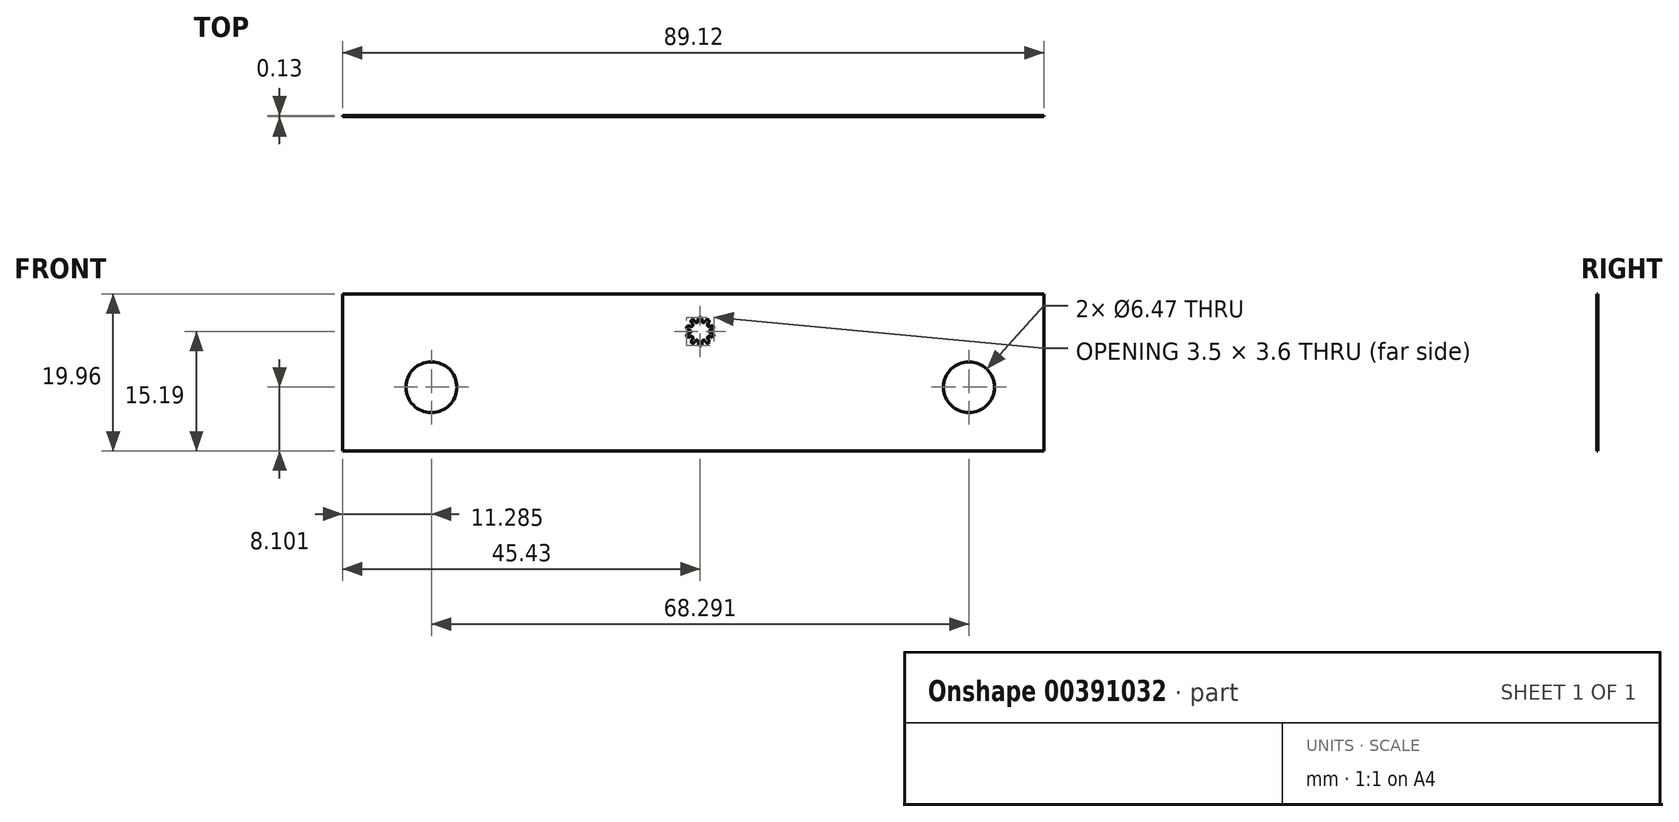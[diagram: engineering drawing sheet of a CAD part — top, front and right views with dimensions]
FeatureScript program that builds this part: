
annotation { "Feature Type Name" : "Feature", "Feature Type Description" : "" }
export const myFeature = defineFeature(function(context is Context, id is Id, definition is map)
    precondition{}
    {
        {
            var Q0;
            Q0=qCreatedBy(makeId("Front.planeOp"),FACE);
            var sketch = newSketch(context, id + "F0", { "sketchPlane" : qUnion([Q0])});
            skLineSegment(sketch, "E0.bottom", {"start": v(-45.43, -15.2) * mm, "end": v(43.7, -15.2) * mm});
            skLineSegment(sketch, "E0.top", {"start": v(-45.43, 4.77) * mm, "end": v(43.7, 4.77) * mm});
            skLineSegment(sketch, "E0.left", {"start": v(-45.43, -15.2) * mm, "end": v(-45.43, 4.77) * mm});
            skLineSegment(sketch, "E0.right", {"start": v(43.7, -15.2) * mm, "end": v(43.7, 4.77) * mm});
            skCircle(sketch, "E1", {"center": v(-34.15, -7.09) * mm, "radius": 3.24 * mm});
            skCircle(sketch, "E2.MirrorC", {"center": v(34.15, -7.09) * mm, "radius": 3.24 * mm});
            skCircle(sketch, "E3", {"center": v(0, 0) * mm, "radius": 0.5 * mm});
            skLineSegment(sketch, "E4", {"start": v(0.64, 1.31) * mm, "end": v(0.64, 1.3) * mm});
            skLineSegment(sketch, "E5", {"start": v(0.64, 1.3) * mm, "end": v(0.64, 1.3) * mm});
            skLineSegment(sketch, "E6", {"start": v(0.64, 1.3) * mm, "end": v(0.63, 1.3) * mm});
            skLineSegment(sketch, "E7", {"start": v(0.63, 1.3) * mm, "end": v(0.63, 1.3) * mm});
            skLineSegment(sketch, "E8", {"start": v(0.63, 1.3) * mm, "end": v(0.62, 1.29) * mm});
            skLineSegment(sketch, "E9", {"start": v(0.62, 1.29) * mm, "end": v(0.62, 1.28) * mm});
            skLineSegment(sketch, "E10", {"start": v(0.62, 1.28) * mm, "end": v(0.62, 1.28) * mm});
            skLineSegment(sketch, "E11", {"start": v(0.62, 1.28) * mm, "end": v(0.61, 1.27) * mm});
            skLineSegment(sketch, "E12", {"start": v(0.61, 1.27) * mm, "end": v(0.61, 1.27) * mm});
            skLineSegment(sketch, "E13", {"start": v(0.61, 1.27) * mm, "end": v(0.54, 1.16) * mm});
            skArc(sketch, "E14", {"start": v(0.54, 1.16) * mm, "mid": v(0.48, 1.12) * mm, "end": v(0.42, 1.12) * mm});
            skArc(sketch, "E15", {"start": v(0.42, 1.12) * mm, "mid": v(0.36, 1.15) * mm, "end": v(0.3, 1.16) * mm});
            skArc(sketch, "E16", {"start": v(0.3, 1.16) * mm, "mid": v(0.24, 1.2) * mm, "end": v(0.22, 1.26) * mm});
            skLineSegment(sketch, "E17", {"start": v(0.22, 1.26) * mm, "end": v(0.22, 1.4) * mm});
            skLineSegment(sketch, "E18", {"start": v(0.22, 1.4) * mm, "end": v(0.22, 1.4) * mm});
            skLineSegment(sketch, "E19", {"start": v(0.22, 1.4) * mm, "end": v(0.22, 1.41) * mm});
            skLineSegment(sketch, "E20", {"start": v(0.22, 1.41) * mm, "end": v(0.22, 1.42) * mm});
            skLineSegment(sketch, "E21", {"start": v(0.22, 1.42) * mm, "end": v(0.22, 1.42) * mm});
            skLineSegment(sketch, "E22", {"start": v(0.22, 1.42) * mm, "end": v(0.22, 1.43) * mm});
            skLineSegment(sketch, "E23", {"start": v(0.22, 1.43) * mm, "end": v(0.22, 1.43) * mm});
            skLineSegment(sketch, "E24", {"start": v(0.22, 1.43) * mm, "end": v(0.22, 1.44) * mm});
            skLineSegment(sketch, "E25", {"start": v(0.22, 1.44) * mm, "end": v(0.22, 1.44) * mm});
            skLineSegment(sketch, "E26", {"start": v(0.22, 1.44) * mm, "end": v(0.22, 1.45) * mm});
            skLineSegment(sketch, "E27", {"start": v(0.22, 1.45) * mm, "end": v(0.22, 1.46) * mm});
            skLineSegment(sketch, "E28", {"start": v(0.22, 1.46) * mm, "end": v(0.22, 1.46) * mm});
            skLineSegment(sketch, "E29", {"start": v(0.22, 1.46) * mm, "end": v(0.22, 1.47) * mm});
            skLineSegment(sketch, "E30", {"start": v(0.22, 1.47) * mm, "end": v(0.22, 1.47) * mm});
            skLineSegment(sketch, "E31", {"start": v(0.22, 1.47) * mm, "end": v(0.22, 1.48) * mm});
            skLineSegment(sketch, "E32", {"start": v(0.22, 1.48) * mm, "end": v(0.22, 1.49) * mm});
            skLineSegment(sketch, "E33", {"start": v(0.22, 1.49) * mm, "end": v(0.22, 1.5) * mm});
            skLineSegment(sketch, "E34", {"start": v(0.22, 1.5) * mm, "end": v(0.22, 1.5) * mm});
            skLineSegment(sketch, "E35", {"start": v(0.22, 1.5) * mm, "end": v(0.22, 1.51) * mm});
            skLineSegment(sketch, "E36", {"start": v(0.22, 1.51) * mm, "end": v(0.22, 1.52) * mm});
            skLineSegment(sketch, "E37", {"start": v(0.22, 1.52) * mm, "end": v(0.22, 1.53) * mm});
            skLineSegment(sketch, "E38", {"start": v(0.22, 1.53) * mm, "end": v(0.22, 1.54) * mm});
            skLineSegment(sketch, "E39", {"start": v(0.22, 1.54) * mm, "end": v(0.21, 1.55) * mm});
            skLineSegment(sketch, "E40", {"start": v(0.21, 1.55) * mm, "end": v(0.21, 1.56) * mm});
            skLineSegment(sketch, "E41", {"start": v(0.21, 1.56) * mm, "end": v(0.2, 1.57) * mm});
            skLineSegment(sketch, "E42", {"start": v(0.2, 1.57) * mm, "end": v(0.2, 1.58) * mm});
            skLineSegment(sketch, "E43", {"start": v(0.2, 1.58) * mm, "end": v(0.2, 1.59) * mm});
            skLineSegment(sketch, "E44", {"start": v(0.2, 1.59) * mm, "end": v(0.2, 1.6) * mm});
            skLineSegment(sketch, "E45", {"start": v(0.2, 1.6) * mm, "end": v(0.2, 1.61) * mm});
            skLineSegment(sketch, "E46", {"start": v(0.2, 1.61) * mm, "end": v(0.19, 1.62) * mm});
            skLineSegment(sketch, "E47", {"start": v(0.19, 1.62) * mm, "end": v(0.18, 1.64) * mm});
            skLineSegment(sketch, "E48", {"start": v(0.18, 1.64) * mm, "end": v(0.17, 1.65) * mm});
            skLineSegment(sketch, "E49", {"start": v(0.17, 1.65) * mm, "end": v(0.17, 1.67) * mm});
            skLineSegment(sketch, "E50", {"start": v(0.17, 1.67) * mm, "end": v(0.16, 1.7) * mm});
            skLineSegment(sketch, "E51", {"start": v(0.16, 1.7) * mm, "end": v(0.14, 1.71) * mm});
            skLineSegment(sketch, "E52", {"start": v(0.14, 1.71) * mm, "end": v(0.13, 1.74) * mm});
            skLineSegment(sketch, "E53", {"start": v(0.13, 1.74) * mm, "end": v(0.1, 1.77) * mm});
            skLineSegment(sketch, "E54", {"start": v(0.1, 1.77) * mm, "end": v(0.1, 1.8) * mm});
            skArc(sketch, "E55", {"start": v(0.1, 1.8) * mm, "mid": v(-0.02, 1.8) * mm, "end": v(-0.13, 1.8) * mm});
            skLineSegment(sketch, "E56", {"start": v(-0.13, 1.8) * mm, "end": v(-0.15, 1.77) * mm});
            skLineSegment(sketch, "E57", {"start": v(-0.15, 1.77) * mm, "end": v(-0.17, 1.74) * mm});
            skLineSegment(sketch, "E58", {"start": v(-0.17, 1.74) * mm, "end": v(-0.18, 1.7) * mm});
            skLineSegment(sketch, "E59", {"start": v(-0.18, 1.7) * mm, "end": v(-0.2, 1.69) * mm});
            skLineSegment(sketch, "E60", {"start": v(-0.2, 1.69) * mm, "end": v(-0.2, 1.67) * mm});
            skLineSegment(sketch, "E61", {"start": v(-0.2, 1.67) * mm, "end": v(-0.21, 1.65) * mm});
            skLineSegment(sketch, "E62", {"start": v(-0.21, 1.65) * mm, "end": v(-0.22, 1.63) * mm});
            skLineSegment(sketch, "E63", {"start": v(-0.22, 1.63) * mm, "end": v(-0.22, 1.62) * mm});
            skLineSegment(sketch, "E64", {"start": v(-0.22, 1.62) * mm, "end": v(-0.23, 1.6) * mm});
            skLineSegment(sketch, "E65", {"start": v(-0.23, 1.6) * mm, "end": v(-0.23, 1.6) * mm});
            skLineSegment(sketch, "E66", {"start": v(-0.23, 1.6) * mm, "end": v(-0.24, 1.58) * mm});
            skLineSegment(sketch, "E67", {"start": v(-0.24, 1.58) * mm, "end": v(-0.24, 1.57) * mm});
            skLineSegment(sketch, "E68", {"start": v(-0.24, 1.57) * mm, "end": v(-0.24, 1.56) * mm});
            skLineSegment(sketch, "E69", {"start": v(-0.24, 1.56) * mm, "end": v(-0.25, 1.55) * mm});
            skLineSegment(sketch, "E70", {"start": v(-0.25, 1.55) * mm, "end": v(-0.25, 1.54) * mm});
            skLineSegment(sketch, "E71", {"start": v(-0.25, 1.54) * mm, "end": v(-0.25, 1.53) * mm});
            skLineSegment(sketch, "E72", {"start": v(-0.25, 1.53) * mm, "end": v(-0.25, 1.53) * mm});
            skLineSegment(sketch, "E73", {"start": v(-0.25, 1.53) * mm, "end": v(-0.25, 1.52) * mm});
            skLineSegment(sketch, "E74", {"start": v(-0.25, 1.52) * mm, "end": v(-0.25, 1.5) * mm});
            skLineSegment(sketch, "E75", {"start": v(-0.25, 1.5) * mm, "end": v(-0.25, 1.5) * mm});
            skLineSegment(sketch, "E76", {"start": v(-0.25, 1.5) * mm, "end": v(-0.25, 1.48) * mm});
            skLineSegment(sketch, "E77", {"start": v(-0.25, 1.48) * mm, "end": v(-0.25, 1.48) * mm});
            skLineSegment(sketch, "E78", {"start": v(-0.25, 1.48) * mm, "end": v(-0.25, 1.47) * mm});
            skLineSegment(sketch, "E79", {"start": v(-0.25, 1.47) * mm, "end": v(-0.25, 1.46) * mm});
            skLineSegment(sketch, "E80", {"start": v(-0.25, 1.46) * mm, "end": v(-0.25, 1.46) * mm});
            skLineSegment(sketch, "E81", {"start": v(-0.25, 1.46) * mm, "end": v(-0.25, 1.45) * mm});
            skLineSegment(sketch, "E82", {"start": v(-0.25, 1.45) * mm, "end": v(-0.25, 1.44) * mm});
            skLineSegment(sketch, "E83", {"start": v(-0.25, 1.44) * mm, "end": v(-0.25, 1.44) * mm});
            skLineSegment(sketch, "E84", {"start": v(-0.25, 1.44) * mm, "end": v(-0.25, 1.43) * mm});
            skLineSegment(sketch, "E85", {"start": v(-0.25, 1.43) * mm, "end": v(-0.25, 1.43) * mm});
            skLineSegment(sketch, "E86", {"start": v(-0.25, 1.43) * mm, "end": v(-0.25, 1.42) * mm});
            skLineSegment(sketch, "E87", {"start": v(-0.25, 1.42) * mm, "end": v(-0.25, 1.42) * mm});
            skLineSegment(sketch, "E88", {"start": v(-0.25, 1.42) * mm, "end": v(-0.25, 1.41) * mm});
            skLineSegment(sketch, "E89", {"start": v(-0.25, 1.41) * mm, "end": v(-0.25, 1.4) * mm});
            skLineSegment(sketch, "E90", {"start": v(-0.25, 1.4) * mm, "end": v(-0.25, 1.4) * mm});
            skLineSegment(sketch, "E91", {"start": v(-0.25, 1.4) * mm, "end": v(-0.25, 1.39) * mm});
            skLineSegment(sketch, "E92", {"start": v(-0.25, 1.39) * mm, "end": v(-0.25, 1.25) * mm});
            skArc(sketch, "E93", {"start": v(-0.25, 1.25) * mm, "mid": v(-0.27, 1.2) * mm, "end": v(-0.32, 1.16) * mm});
            skArc(sketch, "E94", {"start": v(-0.32, 1.16) * mm, "mid": v(-0.38, 1.14) * mm, "end": v(-0.44, 1.11) * mm});
            skArc(sketch, "E95", {"start": v(-0.44, 1.11) * mm, "mid": v(-0.5, 1.11) * mm, "end": v(-0.56, 1.15) * mm});
            skLineSegment(sketch, "E96", {"start": v(-0.56, 1.15) * mm, "end": v(-0.64, 1.25) * mm});
            skLineSegment(sketch, "E97", {"start": v(-0.64, 1.25) * mm, "end": v(-0.64, 1.26) * mm});
            skLineSegment(sketch, "E98", {"start": v(-0.64, 1.26) * mm, "end": v(-0.64, 1.26) * mm});
            skLineSegment(sketch, "E99", {"start": v(-0.64, 1.26) * mm, "end": v(-0.65, 1.26) * mm});
            skLineSegment(sketch, "E100", {"start": v(-0.65, 1.26) * mm, "end": v(-0.65, 1.27) * mm});
            skLineSegment(sketch, "E101", {"start": v(-0.65, 1.27) * mm, "end": v(-0.65, 1.27) * mm});
            skLineSegment(sketch, "E102", {"start": v(-0.65, 1.27) * mm, "end": v(-0.65, 1.28) * mm});
            skLineSegment(sketch, "E103", {"start": v(-0.65, 1.28) * mm, "end": v(-0.66, 1.28) * mm});
            skLineSegment(sketch, "E104", {"start": v(-0.66, 1.28) * mm, "end": v(-0.66, 1.28) * mm});
            skLineSegment(sketch, "E105", {"start": v(-0.66, 1.28) * mm, "end": v(-0.66, 1.29) * mm});
            skLineSegment(sketch, "E106", {"start": v(-0.66, 1.29) * mm, "end": v(-0.67, 1.3) * mm});
            skLineSegment(sketch, "E107", {"start": v(-0.67, 1.3) * mm, "end": v(-0.67, 1.3) * mm});
            skLineSegment(sketch, "E108", {"start": v(-0.67, 1.3) * mm, "end": v(-0.68, 1.3) * mm});
            skLineSegment(sketch, "E109", {"start": v(-0.68, 1.3) * mm, "end": v(-0.68, 1.31) * mm});
            skLineSegment(sketch, "E110", {"start": v(-0.68, 1.31) * mm, "end": v(-0.69, 1.32) * mm});
            skLineSegment(sketch, "E111", {"start": v(-0.69, 1.32) * mm, "end": v(-0.7, 1.32) * mm});
            skLineSegment(sketch, "E112", {"start": v(-0.7, 1.32) * mm, "end": v(-0.7, 1.33) * mm});
            skLineSegment(sketch, "E113", {"start": v(-0.7, 1.33) * mm, "end": v(-0.7, 1.33) * mm});
            skLineSegment(sketch, "E114", {"start": v(-0.7, 1.33) * mm, "end": v(-0.7, 1.34) * mm});
            skLineSegment(sketch, "E115", {"start": v(-0.7, 1.34) * mm, "end": v(-0.7, 1.35) * mm});
            skLineSegment(sketch, "E116", {"start": v(-0.7, 1.35) * mm, "end": v(-0.71, 1.35) * mm});
            skLineSegment(sketch, "E117", {"start": v(-0.71, 1.35) * mm, "end": v(-0.72, 1.36) * mm});
            skLineSegment(sketch, "E118", {"start": v(-0.72, 1.36) * mm, "end": v(-0.72, 1.37) * mm});
            skLineSegment(sketch, "E119", {"start": v(-0.72, 1.37) * mm, "end": v(-0.73, 1.37) * mm});
            skLineSegment(sketch, "E120", {"start": v(-0.73, 1.37) * mm, "end": v(-0.74, 1.38) * mm});
            skLineSegment(sketch, "E121", {"start": v(-0.74, 1.38) * mm, "end": v(-0.74, 1.39) * mm});
            skLineSegment(sketch, "E122", {"start": v(-0.74, 1.39) * mm, "end": v(-0.75, 1.4) * mm});
            skLineSegment(sketch, "E123", {"start": v(-0.75, 1.4) * mm, "end": v(-0.76, 1.4) * mm});
            skLineSegment(sketch, "E124", {"start": v(-0.76, 1.4) * mm, "end": v(-0.77, 1.4) * mm});
            skLineSegment(sketch, "E125", {"start": v(-0.77, 1.4) * mm, "end": v(-0.78, 1.41) * mm});
            skLineSegment(sketch, "E126", {"start": v(-0.78, 1.41) * mm, "end": v(-0.8, 1.42) * mm});
            skLineSegment(sketch, "E127", {"start": v(-0.8, 1.42) * mm, "end": v(-0.8, 1.42) * mm});
            skLineSegment(sketch, "E128", {"start": v(-0.8, 1.42) * mm, "end": v(-0.82, 1.43) * mm});
            skLineSegment(sketch, "E129", {"start": v(-0.82, 1.43) * mm, "end": v(-0.83, 1.44) * mm});
            skLineSegment(sketch, "E130", {"start": v(-0.83, 1.44) * mm, "end": v(-0.85, 1.45) * mm});
            skLineSegment(sketch, "E131", {"start": v(-0.85, 1.45) * mm, "end": v(-0.87, 1.46) * mm});
            skLineSegment(sketch, "E132", {"start": v(-0.87, 1.46) * mm, "end": v(-0.9, 1.47) * mm});
            skLineSegment(sketch, "E133", {"start": v(-0.9, 1.47) * mm, "end": v(-0.92, 1.48) * mm});
            skLineSegment(sketch, "E134", {"start": v(-0.92, 1.48) * mm, "end": v(-0.95, 1.5) * mm});
            skLineSegment(sketch, "E135", {"start": v(-0.95, 1.5) * mm, "end": v(-0.98, 1.5) * mm});
            skArc(sketch, "E136", {"start": v(-0.98, 1.5) * mm, "mid": v(-1.07, 1.44) * mm, "end": v(-1.16, 1.38) * mm});
            skLineSegment(sketch, "E137", {"start": v(-1.16, 1.38) * mm, "end": v(-1.16, 1.34) * mm});
            skLineSegment(sketch, "E138", {"start": v(-1.16, 1.34) * mm, "end": v(-1.15, 1.3) * mm});
            skLineSegment(sketch, "E139", {"start": v(-1.15, 1.3) * mm, "end": v(-1.15, 1.28) * mm});
            skLineSegment(sketch, "E140", {"start": v(-1.15, 1.28) * mm, "end": v(-1.15, 1.25) * mm});
            skLineSegment(sketch, "E141", {"start": v(-1.15, 1.25) * mm, "end": v(-1.14, 1.23) * mm});
            skLineSegment(sketch, "E142", {"start": v(-1.14, 1.23) * mm, "end": v(-1.14, 1.21) * mm});
            skLineSegment(sketch, "E143", {"start": v(-1.14, 1.21) * mm, "end": v(-1.14, 1.2) * mm});
            skLineSegment(sketch, "E144", {"start": v(-1.14, 1.2) * mm, "end": v(-1.13, 1.18) * mm});
            skLineSegment(sketch, "E145", {"start": v(-1.13, 1.18) * mm, "end": v(-1.13, 1.17) * mm});
            skLineSegment(sketch, "E146", {"start": v(-1.13, 1.17) * mm, "end": v(-1.13, 1.15) * mm});
            skLineSegment(sketch, "E147", {"start": v(-1.13, 1.15) * mm, "end": v(-1.12, 1.14) * mm});
            skLineSegment(sketch, "E148", {"start": v(-1.12, 1.14) * mm, "end": v(-1.12, 1.13) * mm});
            skLineSegment(sketch, "E149", {"start": v(-1.12, 1.13) * mm, "end": v(-1.12, 1.12) * mm});
            skLineSegment(sketch, "E150", {"start": v(-1.12, 1.12) * mm, "end": v(-1.11, 1.11) * mm});
            skLineSegment(sketch, "E151", {"start": v(-1.11, 1.11) * mm, "end": v(-1.1, 1.1) * mm});
            skLineSegment(sketch, "E152", {"start": v(-1.1, 1.1) * mm, "end": v(-1.1, 1.1) * mm});
            skLineSegment(sketch, "E153", {"start": v(-1.1, 1.1) * mm, "end": v(-1.1, 1.09) * mm});
            skLineSegment(sketch, "E154", {"start": v(-1.1, 1.09) * mm, "end": v(-1.1, 1.08) * mm});
            skLineSegment(sketch, "E155", {"start": v(-1.1, 1.08) * mm, "end": v(-1.1, 1.07) * mm});
            skLineSegment(sketch, "E156", {"start": v(-1.1, 1.07) * mm, "end": v(-1.09, 1.07) * mm});
            skLineSegment(sketch, "E157", {"start": v(-1.09, 1.07) * mm, "end": v(-1.08, 1.06) * mm});
            skLineSegment(sketch, "E158", {"start": v(-1.08, 1.06) * mm, "end": v(-1.08, 1.05) * mm});
            skLineSegment(sketch, "E159", {"start": v(-1.08, 1.05) * mm, "end": v(-1.07, 1.05) * mm});
            skLineSegment(sketch, "E160", {"start": v(-1.07, 1.05) * mm, "end": v(-1.07, 1.04) * mm});
            skLineSegment(sketch, "E161", {"start": v(-1.07, 1.04) * mm, "end": v(-1.06, 1.04) * mm});
            skLineSegment(sketch, "E162", {"start": v(-1.06, 1.04) * mm, "end": v(-1.06, 1.03) * mm});
            skLineSegment(sketch, "E163", {"start": v(-1.06, 1.03) * mm, "end": v(-1.06, 1.03) * mm});
            skLineSegment(sketch, "E164", {"start": v(-1.06, 1.03) * mm, "end": v(-1.05, 1.02) * mm});
            skLineSegment(sketch, "E165", {"start": v(-1.05, 1.02) * mm, "end": v(-1.05, 1.02) * mm});
            skLineSegment(sketch, "E166", {"start": v(-1.05, 1.02) * mm, "end": v(-1.05, 1.01) * mm});
            skLineSegment(sketch, "E167", {"start": v(-1.05, 1.01) * mm, "end": v(-1.04, 1) * mm});
            skLineSegment(sketch, "E168", {"start": v(-1.04, 1) * mm, "end": v(-1.04, 1) * mm});
            skLineSegment(sketch, "E169", {"start": v(-1.04, 1) * mm, "end": v(-1.03, 1) * mm});
            skLineSegment(sketch, "E170", {"start": v(-1.03, 1) * mm, "end": v(-1.03, 1) * mm});
            skLineSegment(sketch, "E171", {"start": v(-1.03, 1) * mm, "end": v(-1.03, 0.99) * mm});
            skLineSegment(sketch, "E172", {"start": v(-1.03, 0.99) * mm, "end": v(-1.02, 0.98) * mm});
            skLineSegment(sketch, "E173", {"start": v(-1.02, 0.98) * mm, "end": v(-1.02, 0.98) * mm});
            skLineSegment(sketch, "E174", {"start": v(-1.02, 0.98) * mm, "end": v(-1.02, 0.97) * mm});
            skLineSegment(sketch, "E175", {"start": v(-1.02, 0.97) * mm, "end": v(-0.94, 0.87) * mm});
            skArc(sketch, "E176", {"start": v(-0.94, 0.87) * mm, "mid": v(-0.92, 0.8) * mm, "end": v(-0.94, 0.75) * mm});
            skArc(sketch, "E177", {"start": v(-0.94, 0.75) * mm, "mid": v(-0.98, 0.7) * mm, "end": v(-1.01, 0.64) * mm});
            skArc(sketch, "E178", {"start": v(-1.01, 0.64) * mm, "mid": v(-1.06, 0.6) * mm, "end": v(-1.13, 0.6) * mm});
            skLineSegment(sketch, "E179", {"start": v(-1.13, 0.6) * mm, "end": v(-1.26, 0.64) * mm});
            skLineSegment(sketch, "E180", {"start": v(-1.26, 0.64) * mm, "end": v(-1.26, 0.64) * mm});
            skLineSegment(sketch, "E181", {"start": v(-1.26, 0.64) * mm, "end": v(-1.27, 0.64) * mm});
            skLineSegment(sketch, "E182", {"start": v(-1.27, 0.64) * mm, "end": v(-1.27, 0.64) * mm});
            skLineSegment(sketch, "E183", {"start": v(-1.27, 0.64) * mm, "end": v(-1.28, 0.65) * mm});
            skLineSegment(sketch, "E184", {"start": v(-1.28, 0.65) * mm, "end": v(-1.28, 0.65) * mm});
            skLineSegment(sketch, "E185", {"start": v(-1.28, 0.65) * mm, "end": v(-1.29, 0.65) * mm});
            skLineSegment(sketch, "E186", {"start": v(-1.29, 0.65) * mm, "end": v(-1.3, 0.65) * mm});
            skLineSegment(sketch, "E187", {"start": v(-1.3, 0.65) * mm, "end": v(-1.3, 0.65) * mm});
            skLineSegment(sketch, "E188", {"start": v(-1.3, 0.65) * mm, "end": v(-1.3, 0.66) * mm});
            skLineSegment(sketch, "E189", {"start": v(-1.3, 0.66) * mm, "end": v(-1.31, 0.66) * mm});
            skLineSegment(sketch, "E190", {"start": v(-1.31, 0.66) * mm, "end": v(-1.32, 0.66) * mm});
            skLineSegment(sketch, "E191", {"start": v(-1.32, 0.66) * mm, "end": v(-1.32, 0.66) * mm});
            skLineSegment(sketch, "E192", {"start": v(-1.32, 0.66) * mm, "end": v(-1.33, 0.66) * mm});
            skLineSegment(sketch, "E193", {"start": v(-1.33, 0.66) * mm, "end": v(-1.34, 0.66) * mm});
            skLineSegment(sketch, "E194", {"start": v(-1.34, 0.66) * mm, "end": v(-1.34, 0.67) * mm});
            skLineSegment(sketch, "E195", {"start": v(-1.34, 0.67) * mm, "end": v(-1.35, 0.67) * mm});
            skLineSegment(sketch, "E196", {"start": v(-1.35, 0.67) * mm, "end": v(-1.36, 0.67) * mm});
            skLineSegment(sketch, "E197", {"start": v(-1.36, 0.67) * mm, "end": v(-1.36, 0.67) * mm});
            skLineSegment(sketch, "E198", {"start": v(-1.36, 0.67) * mm, "end": v(-1.37, 0.68) * mm});
            skLineSegment(sketch, "E199", {"start": v(-1.37, 0.68) * mm, "end": v(-1.38, 0.68) * mm});
            skLineSegment(sketch, "E200", {"start": v(-1.38, 0.68) * mm, "end": v(-1.39, 0.68) * mm});
            skLineSegment(sketch, "E201", {"start": v(-1.39, 0.68) * mm, "end": v(-1.4, 0.68) * mm});
            skLineSegment(sketch, "E202", {"start": v(-1.4, 0.68) * mm, "end": v(-1.4, 0.68) * mm});
            skLineSegment(sketch, "E203", {"start": v(-1.4, 0.68) * mm, "end": v(-1.42, 0.68) * mm});
            skLineSegment(sketch, "E204", {"start": v(-1.42, 0.68) * mm, "end": v(-1.43, 0.68) * mm});
            skLineSegment(sketch, "E205", {"start": v(-1.43, 0.68) * mm, "end": v(-1.44, 0.68) * mm});
            skLineSegment(sketch, "E206", {"start": v(-1.44, 0.68) * mm, "end": v(-1.45, 0.68) * mm});
            skLineSegment(sketch, "E207", {"start": v(-1.45, 0.68) * mm, "end": v(-1.46, 0.68) * mm});
            skLineSegment(sketch, "E208", {"start": v(-1.46, 0.68) * mm, "end": v(-1.47, 0.68) * mm});
            skLineSegment(sketch, "E209", {"start": v(-1.47, 0.68) * mm, "end": v(-1.49, 0.68) * mm});
            skLineSegment(sketch, "E210", {"start": v(-1.49, 0.68) * mm, "end": v(-1.5, 0.68) * mm});
            skLineSegment(sketch, "E211", {"start": v(-1.5, 0.68) * mm, "end": v(-1.52, 0.68) * mm});
            skLineSegment(sketch, "E212", {"start": v(-1.52, 0.68) * mm, "end": v(-1.54, 0.67) * mm});
            skLineSegment(sketch, "E213", {"start": v(-1.54, 0.67) * mm, "end": v(-1.56, 0.67) * mm});
            skLineSegment(sketch, "E214", {"start": v(-1.56, 0.67) * mm, "end": v(-1.59, 0.67) * mm});
            skLineSegment(sketch, "E215", {"start": v(-1.59, 0.67) * mm, "end": v(-1.62, 0.66) * mm});
            skLineSegment(sketch, "E216", {"start": v(-1.62, 0.66) * mm, "end": v(-1.65, 0.65) * mm});
            skLineSegment(sketch, "E217", {"start": v(-1.65, 0.65) * mm, "end": v(-1.68, 0.64) * mm});
            skArc(sketch, "E218", {"start": v(-1.68, 0.64) * mm, "mid": v(-1.72, 0.54) * mm, "end": v(-1.75, 0.43) * mm});
            skLineSegment(sketch, "E219", {"start": v(-1.75, 0.43) * mm, "end": v(-1.73, 0.4) * mm});
            skLineSegment(sketch, "E220", {"start": v(-1.73, 0.4) * mm, "end": v(-1.7, 0.38) * mm});
            skLineSegment(sketch, "E221", {"start": v(-1.7, 0.38) * mm, "end": v(-1.68, 0.36) * mm});
            skLineSegment(sketch, "E222", {"start": v(-1.68, 0.36) * mm, "end": v(-1.66, 0.34) * mm});
            skLineSegment(sketch, "E223", {"start": v(-1.66, 0.34) * mm, "end": v(-1.65, 0.32) * mm});
            skLineSegment(sketch, "E224", {"start": v(-1.65, 0.32) * mm, "end": v(-1.63, 0.3) * mm});
            skLineSegment(sketch, "E225", {"start": v(-1.63, 0.3) * mm, "end": v(-1.62, 0.3) * mm});
            skLineSegment(sketch, "E226", {"start": v(-1.62, 0.3) * mm, "end": v(-1.61, 0.29) * mm});
            skLineSegment(sketch, "E227", {"start": v(-1.61, 0.29) * mm, "end": v(-1.6, 0.28) * mm});
            skLineSegment(sketch, "E228", {"start": v(-1.6, 0.28) * mm, "end": v(-1.59, 0.27) * mm});
            skLineSegment(sketch, "E229", {"start": v(-1.59, 0.27) * mm, "end": v(-1.58, 0.26) * mm});
            skLineSegment(sketch, "E230", {"start": v(-1.58, 0.26) * mm, "end": v(-1.57, 0.26) * mm});
            skLineSegment(sketch, "E231", {"start": v(-1.57, 0.26) * mm, "end": v(-1.56, 0.25) * mm});
            skLineSegment(sketch, "E232", {"start": v(-1.56, 0.25) * mm, "end": v(-1.55, 0.25) * mm});
            skLineSegment(sketch, "E233", {"start": v(-1.55, 0.25) * mm, "end": v(-1.54, 0.24) * mm});
            skLineSegment(sketch, "E234", {"start": v(-1.54, 0.24) * mm, "end": v(-1.54, 0.24) * mm});
            skLineSegment(sketch, "E235", {"start": v(-1.54, 0.24) * mm, "end": v(-1.53, 0.23) * mm});
            skLineSegment(sketch, "E236", {"start": v(-1.53, 0.23) * mm, "end": v(-1.52, 0.23) * mm});
            skLineSegment(sketch, "E237", {"start": v(-1.52, 0.23) * mm, "end": v(-1.51, 0.23) * mm});
            skLineSegment(sketch, "E238", {"start": v(-1.51, 0.23) * mm, "end": v(-1.5, 0.22) * mm});
            skLineSegment(sketch, "E239", {"start": v(-1.5, 0.22) * mm, "end": v(-1.5, 0.22) * mm});
            skLineSegment(sketch, "E240", {"start": v(-1.5, 0.22) * mm, "end": v(-1.49, 0.22) * mm});
            skLineSegment(sketch, "E241", {"start": v(-1.49, 0.22) * mm, "end": v(-1.48, 0.22) * mm});
            skLineSegment(sketch, "E242", {"start": v(-1.48, 0.22) * mm, "end": v(-1.48, 0.22) * mm});
            skLineSegment(sketch, "E243", {"start": v(-1.48, 0.22) * mm, "end": v(-1.47, 0.21) * mm});
            skLineSegment(sketch, "E244", {"start": v(-1.47, 0.21) * mm, "end": v(-1.46, 0.21) * mm});
            skLineSegment(sketch, "E245", {"start": v(-1.46, 0.21) * mm, "end": v(-1.46, 0.2) * mm});
            skLineSegment(sketch, "E246", {"start": v(-1.46, 0.2) * mm, "end": v(-1.45, 0.2) * mm});
            skLineSegment(sketch, "E247", {"start": v(-1.45, 0.2) * mm, "end": v(-1.45, 0.2) * mm});
            skLineSegment(sketch, "E248", {"start": v(-1.45, 0.2) * mm, "end": v(-1.44, 0.2) * mm});
            skLineSegment(sketch, "E249", {"start": v(-1.44, 0.2) * mm, "end": v(-1.44, 0.2) * mm});
            skLineSegment(sketch, "E250", {"start": v(-1.44, 0.2) * mm, "end": v(-1.43, 0.2) * mm});
            skLineSegment(sketch, "E251", {"start": v(-1.43, 0.2) * mm, "end": v(-1.43, 0.2) * mm});
            skLineSegment(sketch, "E252", {"start": v(-1.43, 0.2) * mm, "end": v(-1.42, 0.2) * mm});
            skLineSegment(sketch, "E253", {"start": v(-1.42, 0.2) * mm, "end": v(-1.42, 0.2) * mm});
            skLineSegment(sketch, "E254", {"start": v(-1.42, 0.2) * mm, "end": v(-1.41, 0.2) * mm});
            skLineSegment(sketch, "E255", {"start": v(-1.41, 0.2) * mm, "end": v(-1.4, 0.2) * mm});
            skLineSegment(sketch, "E256", {"start": v(-1.4, 0.2) * mm, "end": v(-1.4, 0.2) * mm});
            skLineSegment(sketch, "E257", {"start": v(-1.4, 0.2) * mm, "end": v(-1.27, 0.15) * mm});
            skArc(sketch, "E258", {"start": v(-1.27, 0.15) * mm, "mid": v(-1.22, 0.11) * mm, "end": v(-1.2, 0.05) * mm});
            skArc(sketch, "E259", {"start": v(-1.2, 0.05) * mm, "mid": v(-1.2, -0.01) * mm, "end": v(-1.2, -0.08) * mm});
            skArc(sketch, "E260", {"start": v(-1.2, -0.08) * mm, "mid": v(-1.21, -0.14) * mm, "end": v(-1.27, -0.18) * mm});
            skLineSegment(sketch, "E261", {"start": v(-1.27, -0.18) * mm, "end": v(-1.4, -0.22) * mm});
            skLineSegment(sketch, "E262", {"start": v(-1.4, -0.22) * mm, "end": v(-1.4, -0.22) * mm});
            skLineSegment(sketch, "E263", {"start": v(-1.4, -0.22) * mm, "end": v(-1.4, -0.23) * mm});
            skLineSegment(sketch, "E264", {"start": v(-1.4, -0.23) * mm, "end": v(-1.41, -0.23) * mm});
            skLineSegment(sketch, "E265", {"start": v(-1.41, -0.23) * mm, "end": v(-1.42, -0.23) * mm});
            skLineSegment(sketch, "E266", {"start": v(-1.42, -0.23) * mm, "end": v(-1.42, -0.23) * mm});
            skLineSegment(sketch, "E267", {"start": v(-1.42, -0.23) * mm, "end": v(-1.43, -0.23) * mm});
            skLineSegment(sketch, "E268", {"start": v(-1.43, -0.23) * mm, "end": v(-1.43, -0.23) * mm});
            skLineSegment(sketch, "E269", {"start": v(-1.43, -0.23) * mm, "end": v(-1.44, -0.24) * mm});
            skLineSegment(sketch, "E270", {"start": v(-1.44, -0.24) * mm, "end": v(-1.44, -0.24) * mm});
            skLineSegment(sketch, "E271", {"start": v(-1.44, -0.24) * mm, "end": v(-1.45, -0.24) * mm});
            skLineSegment(sketch, "E272", {"start": v(-1.45, -0.24) * mm, "end": v(-1.45, -0.24) * mm});
            skLineSegment(sketch, "E273", {"start": v(-1.45, -0.24) * mm, "end": v(-1.46, -0.24) * mm});
            skLineSegment(sketch, "E274", {"start": v(-1.46, -0.24) * mm, "end": v(-1.46, -0.25) * mm});
            skLineSegment(sketch, "E275", {"start": v(-1.46, -0.25) * mm, "end": v(-1.47, -0.25) * mm});
            skLineSegment(sketch, "E276", {"start": v(-1.47, -0.25) * mm, "end": v(-1.48, -0.25) * mm});
            skLineSegment(sketch, "E277", {"start": v(-1.48, -0.25) * mm, "end": v(-1.48, -0.25) * mm});
            skLineSegment(sketch, "E278", {"start": v(-1.48, -0.25) * mm, "end": v(-1.5, -0.25) * mm});
            skLineSegment(sketch, "E279", {"start": v(-1.5, -0.25) * mm, "end": v(-1.5, -0.26) * mm});
            skLineSegment(sketch, "E280", {"start": v(-1.5, -0.26) * mm, "end": v(-1.5, -0.26) * mm});
            skLineSegment(sketch, "E281", {"start": v(-1.5, -0.26) * mm, "end": v(-1.51, -0.26) * mm});
            skLineSegment(sketch, "E282", {"start": v(-1.51, -0.26) * mm, "end": v(-1.52, -0.27) * mm});
            skLineSegment(sketch, "E283", {"start": v(-1.52, -0.27) * mm, "end": v(-1.53, -0.27) * mm});
            skLineSegment(sketch, "E284", {"start": v(-1.53, -0.27) * mm, "end": v(-1.54, -0.27) * mm});
            skLineSegment(sketch, "E285", {"start": v(-1.54, -0.27) * mm, "end": v(-1.55, -0.28) * mm});
            skLineSegment(sketch, "E286", {"start": v(-1.55, -0.28) * mm, "end": v(-1.56, -0.28) * mm});
            skLineSegment(sketch, "E287", {"start": v(-1.56, -0.28) * mm, "end": v(-1.56, -0.3) * mm});
            skLineSegment(sketch, "E288", {"start": v(-1.56, -0.3) * mm, "end": v(-1.57, -0.3) * mm});
            skLineSegment(sketch, "E289", {"start": v(-1.57, -0.3) * mm, "end": v(-1.58, -0.3) * mm});
            skLineSegment(sketch, "E290", {"start": v(-1.58, -0.3) * mm, "end": v(-1.6, -0.31) * mm});
            skLineSegment(sketch, "E291", {"start": v(-1.6, -0.31) * mm, "end": v(-1.6, -0.32) * mm});
            skLineSegment(sketch, "E292", {"start": v(-1.6, -0.32) * mm, "end": v(-1.61, -0.33) * mm});
            skLineSegment(sketch, "E293", {"start": v(-1.61, -0.33) * mm, "end": v(-1.63, -0.35) * mm});
            skLineSegment(sketch, "E294", {"start": v(-1.63, -0.35) * mm, "end": v(-1.64, -0.36) * mm});
            skLineSegment(sketch, "E295", {"start": v(-1.64, -0.36) * mm, "end": v(-1.66, -0.37) * mm});
            skLineSegment(sketch, "E296", {"start": v(-1.66, -0.37) * mm, "end": v(-1.67, -0.4) * mm});
            skLineSegment(sketch, "E297", {"start": v(-1.67, -0.4) * mm, "end": v(-1.7, -0.42) * mm});
            skLineSegment(sketch, "E298", {"start": v(-1.7, -0.42) * mm, "end": v(-1.72, -0.44) * mm});
            skLineSegment(sketch, "E299", {"start": v(-1.72, -0.44) * mm, "end": v(-1.74, -0.47) * mm});
            skArc(sketch, "E300", {"start": v(-1.74, -0.47) * mm, "mid": v(-1.7, -0.57) * mm, "end": v(-1.67, -0.68) * mm});
            skLineSegment(sketch, "E301", {"start": v(-1.67, -0.68) * mm, "end": v(-1.63, -0.69) * mm});
            skLineSegment(sketch, "E302", {"start": v(-1.63, -0.69) * mm, "end": v(-1.6, -0.7) * mm});
            skLineSegment(sketch, "E303", {"start": v(-1.6, -0.7) * mm, "end": v(-1.57, -0.7) * mm});
            skLineSegment(sketch, "E304", {"start": v(-1.57, -0.7) * mm, "end": v(-1.54, -0.7) * mm});
            skLineSegment(sketch, "E305", {"start": v(-1.54, -0.7) * mm, "end": v(-1.52, -0.7) * mm});
            skLineSegment(sketch, "E306", {"start": v(-1.52, -0.7) * mm, "end": v(-1.5, -0.71) * mm});
            skLineSegment(sketch, "E307", {"start": v(-1.5, -0.71) * mm, "end": v(-1.49, -0.71) * mm});
            skLineSegment(sketch, "E308", {"start": v(-1.49, -0.71) * mm, "end": v(-1.47, -0.71) * mm});
            skLineSegment(sketch, "E309", {"start": v(-1.47, -0.71) * mm, "end": v(-1.46, -0.71) * mm});
            skLineSegment(sketch, "E310", {"start": v(-1.46, -0.71) * mm, "end": v(-1.44, -0.71) * mm});
            skLineSegment(sketch, "E311", {"start": v(-1.44, -0.71) * mm, "end": v(-1.43, -0.72) * mm});
            skLineSegment(sketch, "E312", {"start": v(-1.43, -0.72) * mm, "end": v(-1.42, -0.72) * mm});
            skLineSegment(sketch, "E313", {"start": v(-1.42, -0.72) * mm, "end": v(-1.41, -0.72) * mm});
            skLineSegment(sketch, "E314", {"start": v(-1.41, -0.72) * mm, "end": v(-1.4, -0.71) * mm});
            skLineSegment(sketch, "E315", {"start": v(-1.4, -0.71) * mm, "end": v(-1.4, -0.71) * mm});
            skLineSegment(sketch, "E316", {"start": v(-1.4, -0.71) * mm, "end": v(-1.38, -0.71) * mm});
            skLineSegment(sketch, "E317", {"start": v(-1.38, -0.71) * mm, "end": v(-1.37, -0.71) * mm});
            skLineSegment(sketch, "E318", {"start": v(-1.37, -0.71) * mm, "end": v(-1.36, -0.7) * mm});
            skLineSegment(sketch, "E319", {"start": v(-1.36, -0.7) * mm, "end": v(-1.36, -0.7) * mm});
            skLineSegment(sketch, "E320", {"start": v(-1.36, -0.7) * mm, "end": v(-1.35, -0.7) * mm});
            skLineSegment(sketch, "E321", {"start": v(-1.35, -0.7) * mm, "end": v(-1.34, -0.7) * mm});
            skLineSegment(sketch, "E322", {"start": v(-1.34, -0.7) * mm, "end": v(-1.33, -0.7) * mm});
            skLineSegment(sketch, "E323", {"start": v(-1.33, -0.7) * mm, "end": v(-1.33, -0.7) * mm});
            skLineSegment(sketch, "E324", {"start": v(-1.33, -0.7) * mm, "end": v(-1.32, -0.7) * mm});
            skLineSegment(sketch, "E325", {"start": v(-1.32, -0.7) * mm, "end": v(-1.31, -0.7) * mm});
            skLineSegment(sketch, "E326", {"start": v(-1.31, -0.7) * mm, "end": v(-1.3, -0.69) * mm});
            skLineSegment(sketch, "E327", {"start": v(-1.3, -0.69) * mm, "end": v(-1.3, -0.69) * mm});
            skLineSegment(sketch, "E328", {"start": v(-1.3, -0.69) * mm, "end": v(-1.3, -0.68) * mm});
            skLineSegment(sketch, "E329", {"start": v(-1.3, -0.68) * mm, "end": v(-1.29, -0.68) * mm});
            skLineSegment(sketch, "E330", {"start": v(-1.29, -0.68) * mm, "end": v(-1.28, -0.68) * mm});
            skLineSegment(sketch, "E331", {"start": v(-1.28, -0.68) * mm, "end": v(-1.28, -0.68) * mm});
            skLineSegment(sketch, "E332", {"start": v(-1.28, -0.68) * mm, "end": v(-1.27, -0.68) * mm});
            skLineSegment(sketch, "E333", {"start": v(-1.27, -0.68) * mm, "end": v(-1.27, -0.68) * mm});
            skLineSegment(sketch, "E334", {"start": v(-1.27, -0.68) * mm, "end": v(-1.26, -0.67) * mm});
            skLineSegment(sketch, "E335", {"start": v(-1.26, -0.67) * mm, "end": v(-1.26, -0.67) * mm});
            skLineSegment(sketch, "E336", {"start": v(-1.26, -0.67) * mm, "end": v(-1.25, -0.67) * mm});
            skLineSegment(sketch, "E337", {"start": v(-1.25, -0.67) * mm, "end": v(-1.25, -0.67) * mm});
            skLineSegment(sketch, "E338", {"start": v(-1.25, -0.67) * mm, "end": v(-1.24, -0.67) * mm});
            skLineSegment(sketch, "E339", {"start": v(-1.24, -0.67) * mm, "end": v(-1.24, -0.67) * mm});
            skLineSegment(sketch, "E340", {"start": v(-1.24, -0.67) * mm, "end": v(-1.12, -0.62) * mm});
            skArc(sketch, "E341", {"start": v(-1.12, -0.62) * mm, "mid": v(-1.05, -0.62) * mm, "end": v(-1, -0.66) * mm});
            skArc(sketch, "E342", {"start": v(-1, -0.66) * mm, "mid": v(-0.96, -0.72) * mm, "end": v(-0.92, -0.77) * mm});
            skArc(sketch, "E343", {"start": v(-0.92, -0.77) * mm, "mid": v(-0.9, -0.83) * mm, "end": v(-0.92, -0.89) * mm});
            skLineSegment(sketch, "E344", {"start": v(-0.92, -0.89) * mm, "end": v(-1, -1) * mm});
            skLineSegment(sketch, "E345", {"start": v(-1, -1) * mm, "end": v(-1, -1) * mm});
            skLineSegment(sketch, "E346", {"start": v(-1, -1) * mm, "end": v(-1, -1.01) * mm});
            skLineSegment(sketch, "E347", {"start": v(-1, -1.01) * mm, "end": v(-1.01, -1.02) * mm});
            skLineSegment(sketch, "E348", {"start": v(-1.01, -1.02) * mm, "end": v(-1.01, -1.02) * mm});
            skLineSegment(sketch, "E349", {"start": v(-1.01, -1.02) * mm, "end": v(-1.02, -1.03) * mm});
            skLineSegment(sketch, "E350", {"start": v(-1.02, -1.03) * mm, "end": v(-1.02, -1.03) * mm});
            skLineSegment(sketch, "E351", {"start": v(-1.02, -1.03) * mm, "end": v(-1.03, -1.04) * mm});
            skLineSegment(sketch, "E352", {"start": v(-1.03, -1.04) * mm, "end": v(-1.03, -1.04) * mm});
            skLineSegment(sketch, "E353", {"start": v(-1.03, -1.04) * mm, "end": v(-1.03, -1.05) * mm});
            skLineSegment(sketch, "E354", {"start": v(-1.03, -1.05) * mm, "end": v(-1.04, -1.05) * mm});
            skLineSegment(sketch, "E355", {"start": v(-1.04, -1.05) * mm, "end": v(-1.04, -1.06) * mm});
            skLineSegment(sketch, "E356", {"start": v(-1.04, -1.06) * mm, "end": v(-1.04, -1.06) * mm});
            skLineSegment(sketch, "E357", {"start": v(-1.04, -1.06) * mm, "end": v(-1.05, -1.07) * mm});
            skLineSegment(sketch, "E358", {"start": v(-1.05, -1.07) * mm, "end": v(-1.05, -1.08) * mm});
            skLineSegment(sketch, "E359", {"start": v(-1.05, -1.08) * mm, "end": v(-1.06, -1.08) * mm});
            skLineSegment(sketch, "E360", {"start": v(-1.06, -1.08) * mm, "end": v(-1.06, -1.09) * mm});
            skLineSegment(sketch, "E361", {"start": v(-1.06, -1.09) * mm, "end": v(-1.07, -1.1) * mm});
            skLineSegment(sketch, "E362", {"start": v(-1.07, -1.1) * mm, "end": v(-1.07, -1.1) * mm});
            skLineSegment(sketch, "E363", {"start": v(-1.07, -1.1) * mm, "end": v(-1.08, -1.11) * mm});
            skLineSegment(sketch, "E364", {"start": v(-1.08, -1.11) * mm, "end": v(-1.08, -1.12) * mm});
            skLineSegment(sketch, "E365", {"start": v(-1.08, -1.12) * mm, "end": v(-1.08, -1.13) * mm});
            skLineSegment(sketch, "E366", {"start": v(-1.08, -1.13) * mm, "end": v(-1.09, -1.14) * mm});
            skLineSegment(sketch, "E367", {"start": v(-1.09, -1.14) * mm, "end": v(-1.1, -1.14) * mm});
            skLineSegment(sketch, "E368", {"start": v(-1.1, -1.14) * mm, "end": v(-1.1, -1.16) * mm});
            skLineSegment(sketch, "E369", {"start": v(-1.1, -1.16) * mm, "end": v(-1.1, -1.17) * mm});
            skLineSegment(sketch, "E370", {"start": v(-1.1, -1.17) * mm, "end": v(-1.1, -1.18) * mm});
            skLineSegment(sketch, "E371", {"start": v(-1.1, -1.18) * mm, "end": v(-1.1, -1.2) * mm});
            skLineSegment(sketch, "E372", {"start": v(-1.1, -1.2) * mm, "end": v(-1.1, -1.2) * mm});
            skLineSegment(sketch, "E373", {"start": v(-1.1, -1.2) * mm, "end": v(-1.11, -1.22) * mm});
            skLineSegment(sketch, "E374", {"start": v(-1.11, -1.22) * mm, "end": v(-1.11, -1.24) * mm});
            skLineSegment(sketch, "E375", {"start": v(-1.11, -1.24) * mm, "end": v(-1.12, -1.25) * mm});
            skLineSegment(sketch, "E376", {"start": v(-1.12, -1.25) * mm, "end": v(-1.12, -1.28) * mm});
            skLineSegment(sketch, "E377", {"start": v(-1.12, -1.28) * mm, "end": v(-1.12, -1.3) * mm});
            skLineSegment(sketch, "E378", {"start": v(-1.12, -1.3) * mm, "end": v(-1.13, -1.33) * mm});
            skLineSegment(sketch, "E379", {"start": v(-1.13, -1.33) * mm, "end": v(-1.13, -1.37) * mm});
            skLineSegment(sketch, "E380", {"start": v(-1.13, -1.37) * mm, "end": v(-1.13, -1.4) * mm});
            skArc(sketch, "E381", {"start": v(-1.13, -1.4) * mm, "mid": v(-1.04, -1.47) * mm, "end": v(-0.95, -1.53) * mm});
            skLineSegment(sketch, "E382", {"start": v(-0.95, -1.53) * mm, "end": v(-0.92, -1.52) * mm});
            skLineSegment(sketch, "E383", {"start": v(-0.92, -1.52) * mm, "end": v(-0.89, -1.5) * mm});
            skLineSegment(sketch, "E384", {"start": v(-0.89, -1.5) * mm, "end": v(-0.86, -1.49) * mm});
            skLineSegment(sketch, "E385", {"start": v(-0.86, -1.49) * mm, "end": v(-0.84, -1.48) * mm});
            skLineSegment(sketch, "E386", {"start": v(-0.84, -1.48) * mm, "end": v(-0.82, -1.47) * mm});
            skLineSegment(sketch, "E387", {"start": v(-0.82, -1.47) * mm, "end": v(-0.8, -1.46) * mm});
            skLineSegment(sketch, "E388", {"start": v(-0.8, -1.46) * mm, "end": v(-0.78, -1.45) * mm});
            skLineSegment(sketch, "E389", {"start": v(-0.78, -1.45) * mm, "end": v(-0.77, -1.44) * mm});
            skLineSegment(sketch, "E390", {"start": v(-0.77, -1.44) * mm, "end": v(-0.76, -1.43) * mm});
            skLineSegment(sketch, "E391", {"start": v(-0.76, -1.43) * mm, "end": v(-0.75, -1.43) * mm});
            skLineSegment(sketch, "E392", {"start": v(-0.75, -1.43) * mm, "end": v(-0.74, -1.42) * mm});
            skLineSegment(sketch, "E393", {"start": v(-0.74, -1.42) * mm, "end": v(-0.73, -1.41) * mm});
            skLineSegment(sketch, "E394", {"start": v(-0.73, -1.41) * mm, "end": v(-0.72, -1.4) * mm});
            skLineSegment(sketch, "E395", {"start": v(-0.72, -1.4) * mm, "end": v(-0.71, -1.4) * mm});
            skLineSegment(sketch, "E396", {"start": v(-0.71, -1.4) * mm, "end": v(-0.7, -1.4) * mm});
            skLineSegment(sketch, "E397", {"start": v(-0.7, -1.4) * mm, "end": v(-0.7, -1.39) * mm});
            skLineSegment(sketch, "E398", {"start": v(-0.7, -1.39) * mm, "end": v(-0.7, -1.38) * mm});
            skLineSegment(sketch, "E399", {"start": v(-0.7, -1.38) * mm, "end": v(-0.69, -1.37) * mm});
            skLineSegment(sketch, "E400", {"start": v(-0.69, -1.37) * mm, "end": v(-0.68, -1.37) * mm});
            skLineSegment(sketch, "E401", {"start": v(-0.68, -1.37) * mm, "end": v(-0.68, -1.36) * mm});
            skLineSegment(sketch, "E402", {"start": v(-0.68, -1.36) * mm, "end": v(-0.67, -1.35) * mm});
            skLineSegment(sketch, "E403", {"start": v(-0.67, -1.35) * mm, "end": v(-0.67, -1.35) * mm});
            skLineSegment(sketch, "E404", {"start": v(-0.67, -1.35) * mm, "end": v(-0.67, -1.34) * mm});
            skLineSegment(sketch, "E405", {"start": v(-0.67, -1.34) * mm, "end": v(-0.66, -1.34) * mm});
            skLineSegment(sketch, "E406", {"start": v(-0.66, -1.34) * mm, "end": v(-0.66, -1.33) * mm});
            skLineSegment(sketch, "E407", {"start": v(-0.66, -1.33) * mm, "end": v(-0.65, -1.33) * mm});
            skLineSegment(sketch, "E408", {"start": v(-0.65, -1.33) * mm, "end": v(-0.65, -1.32) * mm});
            skLineSegment(sketch, "E409", {"start": v(-0.65, -1.32) * mm, "end": v(-0.65, -1.32) * mm});
            skLineSegment(sketch, "E410", {"start": v(-0.65, -1.32) * mm, "end": v(-0.64, -1.31) * mm});
            skLineSegment(sketch, "E411", {"start": v(-0.64, -1.31) * mm, "end": v(-0.64, -1.3) * mm});
            skLineSegment(sketch, "E412", {"start": v(-0.64, -1.3) * mm, "end": v(-0.64, -1.3) * mm});
            skLineSegment(sketch, "E413", {"start": v(-0.64, -1.3) * mm, "end": v(-0.63, -1.3) * mm});
            skLineSegment(sketch, "E414", {"start": v(-0.63, -1.3) * mm, "end": v(-0.63, -1.3) * mm});
            skLineSegment(sketch, "E415", {"start": v(-0.63, -1.3) * mm, "end": v(-0.62, -1.29) * mm});
            skLineSegment(sketch, "E416", {"start": v(-0.62, -1.29) * mm, "end": v(-0.62, -1.28) * mm});
            skLineSegment(sketch, "E417", {"start": v(-0.62, -1.28) * mm, "end": v(-0.62, -1.28) * mm});
            skLineSegment(sketch, "E418", {"start": v(-0.62, -1.28) * mm, "end": v(-0.61, -1.27) * mm});
            skLineSegment(sketch, "E419", {"start": v(-0.61, -1.27) * mm, "end": v(-0.61, -1.27) * mm});
            skLineSegment(sketch, "E420", {"start": v(-0.61, -1.27) * mm, "end": v(-0.54, -1.16) * mm});
            skArc(sketch, "E421", {"start": v(-0.54, -1.16) * mm, "mid": v(-0.48, -1.12) * mm, "end": v(-0.42, -1.12) * mm});
            skArc(sketch, "E422", {"start": v(-0.42, -1.12) * mm, "mid": v(-0.36, -1.15) * mm, "end": v(-0.3, -1.16) * mm});
            skArc(sketch, "E423", {"start": v(-0.3, -1.16) * mm, "mid": v(-0.24, -1.2) * mm, "end": v(-0.22, -1.26) * mm});
            skLineSegment(sketch, "E424", {"start": v(-0.22, -1.26) * mm, "end": v(-0.22, -1.4) * mm});
            skLineSegment(sketch, "E425", {"start": v(-0.22, -1.4) * mm, "end": v(-0.22, -1.4) * mm});
            skLineSegment(sketch, "E426", {"start": v(-0.22, -1.4) * mm, "end": v(-0.22, -1.41) * mm});
            skLineSegment(sketch, "E427", {"start": v(-0.22, -1.41) * mm, "end": v(-0.22, -1.42) * mm});
            skLineSegment(sketch, "E428", {"start": v(-0.22, -1.42) * mm, "end": v(-0.22, -1.42) * mm});
            skLineSegment(sketch, "E429", {"start": v(-0.22, -1.42) * mm, "end": v(-0.22, -1.43) * mm});
            skLineSegment(sketch, "E430", {"start": v(-0.22, -1.43) * mm, "end": v(-0.22, -1.43) * mm});
            skLineSegment(sketch, "E431", {"start": v(-0.22, -1.43) * mm, "end": v(-0.22, -1.44) * mm});
            skLineSegment(sketch, "E432", {"start": v(-0.22, -1.44) * mm, "end": v(-0.22, -1.44) * mm});
            skLineSegment(sketch, "E433", {"start": v(-0.22, -1.44) * mm, "end": v(-0.22, -1.45) * mm});
            skLineSegment(sketch, "E434", {"start": v(-0.22, -1.45) * mm, "end": v(-0.22, -1.46) * mm});
            skLineSegment(sketch, "E435", {"start": v(-0.22, -1.46) * mm, "end": v(-0.22, -1.46) * mm});
            skLineSegment(sketch, "E436", {"start": v(-0.22, -1.46) * mm, "end": v(-0.22, -1.47) * mm});
            skLineSegment(sketch, "E437", {"start": v(-0.22, -1.47) * mm, "end": v(-0.22, -1.47) * mm});
            skLineSegment(sketch, "E438", {"start": v(-0.22, -1.47) * mm, "end": v(-0.22, -1.48) * mm});
            skLineSegment(sketch, "E439", {"start": v(-0.22, -1.48) * mm, "end": v(-0.22, -1.49) * mm});
            skLineSegment(sketch, "E440", {"start": v(-0.22, -1.49) * mm, "end": v(-0.22, -1.5) * mm});
            skLineSegment(sketch, "E441", {"start": v(-0.22, -1.5) * mm, "end": v(-0.22, -1.5) * mm});
            skLineSegment(sketch, "E442", {"start": v(-0.22, -1.5) * mm, "end": v(-0.22, -1.51) * mm});
            skLineSegment(sketch, "E443", {"start": v(-0.22, -1.51) * mm, "end": v(-0.22, -1.52) * mm});
            skLineSegment(sketch, "E444", {"start": v(-0.22, -1.52) * mm, "end": v(-0.22, -1.53) * mm});
            skLineSegment(sketch, "E445", {"start": v(-0.22, -1.53) * mm, "end": v(-0.22, -1.54) * mm});
            skLineSegment(sketch, "E446", {"start": v(-0.22, -1.54) * mm, "end": v(-0.21, -1.55) * mm});
            skLineSegment(sketch, "E447", {"start": v(-0.21, -1.55) * mm, "end": v(-0.21, -1.56) * mm});
            skLineSegment(sketch, "E448", {"start": v(-0.21, -1.56) * mm, "end": v(-0.2, -1.57) * mm});
            skLineSegment(sketch, "E449", {"start": v(-0.2, -1.57) * mm, "end": v(-0.2, -1.58) * mm});
            skLineSegment(sketch, "E450", {"start": v(-0.2, -1.58) * mm, "end": v(-0.2, -1.59) * mm});
            skLineSegment(sketch, "E451", {"start": v(-0.2, -1.59) * mm, "end": v(-0.2, -1.6) * mm});
            skLineSegment(sketch, "E452", {"start": v(-0.2, -1.6) * mm, "end": v(-0.2, -1.61) * mm});
            skLineSegment(sketch, "E453", {"start": v(-0.2, -1.61) * mm, "end": v(-0.19, -1.62) * mm});
            skLineSegment(sketch, "E454", {"start": v(-0.19, -1.62) * mm, "end": v(-0.18, -1.64) * mm});
            skLineSegment(sketch, "E455", {"start": v(-0.18, -1.64) * mm, "end": v(-0.17, -1.65) * mm});
            skLineSegment(sketch, "E456", {"start": v(-0.17, -1.65) * mm, "end": v(-0.17, -1.67) * mm});
            skLineSegment(sketch, "E457", {"start": v(-0.17, -1.67) * mm, "end": v(-0.16, -1.7) * mm});
            skLineSegment(sketch, "E458", {"start": v(-0.16, -1.7) * mm, "end": v(-0.14, -1.71) * mm});
            skLineSegment(sketch, "E459", {"start": v(-0.14, -1.71) * mm, "end": v(-0.13, -1.74) * mm});
            skLineSegment(sketch, "E460", {"start": v(-0.13, -1.74) * mm, "end": v(-0.1, -1.77) * mm});
            skLineSegment(sketch, "E461", {"start": v(-0.1, -1.77) * mm, "end": v(-0.1, -1.8) * mm});
            skArc(sketch, "E462", {"start": v(-0.1, -1.8) * mm, "mid": v(0.02, -1.8) * mm, "end": v(0.13, -1.8) * mm});
            skLineSegment(sketch, "E463", {"start": v(0.13, -1.8) * mm, "end": v(0.15, -1.77) * mm});
            skLineSegment(sketch, "E464", {"start": v(0.15, -1.77) * mm, "end": v(0.17, -1.74) * mm});
            skLineSegment(sketch, "E465", {"start": v(0.17, -1.74) * mm, "end": v(0.18, -1.7) * mm});
            skLineSegment(sketch, "E466", {"start": v(0.18, -1.7) * mm, "end": v(0.2, -1.69) * mm});
            skLineSegment(sketch, "E467", {"start": v(0.2, -1.69) * mm, "end": v(0.2, -1.67) * mm});
            skLineSegment(sketch, "E468", {"start": v(0.2, -1.67) * mm, "end": v(0.21, -1.65) * mm});
            skLineSegment(sketch, "E469", {"start": v(0.21, -1.65) * mm, "end": v(0.22, -1.63) * mm});
            skLineSegment(sketch, "E470", {"start": v(0.22, -1.63) * mm, "end": v(0.22, -1.62) * mm});
            skLineSegment(sketch, "E471", {"start": v(0.22, -1.62) * mm, "end": v(0.23, -1.6) * mm});
            skLineSegment(sketch, "E472", {"start": v(0.23, -1.6) * mm, "end": v(0.23, -1.6) * mm});
            skLineSegment(sketch, "E473", {"start": v(0.23, -1.6) * mm, "end": v(0.24, -1.58) * mm});
            skLineSegment(sketch, "E474", {"start": v(0.24, -1.58) * mm, "end": v(0.24, -1.57) * mm});
            skLineSegment(sketch, "E475", {"start": v(0.24, -1.57) * mm, "end": v(0.24, -1.56) * mm});
            skLineSegment(sketch, "E476", {"start": v(0.24, -1.56) * mm, "end": v(0.25, -1.55) * mm});
            skLineSegment(sketch, "E477", {"start": v(0.25, -1.55) * mm, "end": v(0.25, -1.54) * mm});
            skLineSegment(sketch, "E478", {"start": v(0.25, -1.54) * mm, "end": v(0.25, -1.53) * mm});
            skLineSegment(sketch, "E479", {"start": v(0.25, -1.53) * mm, "end": v(0.25, -1.53) * mm});
            skLineSegment(sketch, "E480", {"start": v(0.25, -1.53) * mm, "end": v(0.25, -1.52) * mm});
            skLineSegment(sketch, "E481", {"start": v(0.25, -1.52) * mm, "end": v(0.25, -1.5) * mm});
            skLineSegment(sketch, "E482", {"start": v(0.25, -1.5) * mm, "end": v(0.25, -1.5) * mm});
            skLineSegment(sketch, "E483", {"start": v(0.25, -1.5) * mm, "end": v(0.25, -1.48) * mm});
            skLineSegment(sketch, "E484", {"start": v(0.25, -1.48) * mm, "end": v(0.25, -1.48) * mm});
            skLineSegment(sketch, "E485", {"start": v(0.25, -1.48) * mm, "end": v(0.25, -1.47) * mm});
            skLineSegment(sketch, "E486", {"start": v(0.25, -1.47) * mm, "end": v(0.25, -1.46) * mm});
            skLineSegment(sketch, "E487", {"start": v(0.25, -1.46) * mm, "end": v(0.25, -1.46) * mm});
            skLineSegment(sketch, "E488", {"start": v(0.25, -1.46) * mm, "end": v(0.25, -1.45) * mm});
            skLineSegment(sketch, "E489", {"start": v(0.25, -1.45) * mm, "end": v(0.25, -1.44) * mm});
            skLineSegment(sketch, "E490", {"start": v(0.25, -1.44) * mm, "end": v(0.25, -1.44) * mm});
            skLineSegment(sketch, "E491", {"start": v(0.25, -1.44) * mm, "end": v(0.25, -1.43) * mm});
            skLineSegment(sketch, "E492", {"start": v(0.25, -1.43) * mm, "end": v(0.25, -1.43) * mm});
            skLineSegment(sketch, "E493", {"start": v(0.25, -1.43) * mm, "end": v(0.25, -1.42) * mm});
            skLineSegment(sketch, "E494", {"start": v(0.25, -1.42) * mm, "end": v(0.25, -1.42) * mm});
            skLineSegment(sketch, "E495", {"start": v(0.25, -1.42) * mm, "end": v(0.25, -1.41) * mm});
            skLineSegment(sketch, "E496", {"start": v(0.25, -1.41) * mm, "end": v(0.25, -1.4) * mm});
            skLineSegment(sketch, "E497", {"start": v(0.25, -1.4) * mm, "end": v(0.25, -1.4) * mm});
            skLineSegment(sketch, "E498", {"start": v(0.25, -1.4) * mm, "end": v(0.25, -1.39) * mm});
            skLineSegment(sketch, "E499", {"start": v(0.25, -1.39) * mm, "end": v(0.25, -1.25) * mm});
            skArc(sketch, "E500", {"start": v(0.25, -1.25) * mm, "mid": v(0.27, -1.2) * mm, "end": v(0.32, -1.16) * mm});
            skArc(sketch, "E501", {"start": v(0.32, -1.16) * mm, "mid": v(0.38, -1.14) * mm, "end": v(0.44, -1.11) * mm});
            skArc(sketch, "E502", {"start": v(0.44, -1.11) * mm, "mid": v(0.5, -1.11) * mm, "end": v(0.56, -1.15) * mm});
            skLineSegment(sketch, "E503", {"start": v(0.56, -1.15) * mm, "end": v(0.64, -1.25) * mm});
            skLineSegment(sketch, "E504", {"start": v(0.64, -1.25) * mm, "end": v(0.64, -1.26) * mm});
            skLineSegment(sketch, "E505", {"start": v(0.64, -1.26) * mm, "end": v(0.64, -1.26) * mm});
            skLineSegment(sketch, "E506", {"start": v(0.64, -1.26) * mm, "end": v(0.65, -1.26) * mm});
            skLineSegment(sketch, "E507", {"start": v(0.65, -1.26) * mm, "end": v(0.65, -1.27) * mm});
            skLineSegment(sketch, "E508", {"start": v(0.65, -1.27) * mm, "end": v(0.65, -1.27) * mm});
            skLineSegment(sketch, "E509", {"start": v(0.65, -1.27) * mm, "end": v(0.65, -1.28) * mm});
            skLineSegment(sketch, "E510", {"start": v(0.65, -1.28) * mm, "end": v(0.66, -1.28) * mm});
            skLineSegment(sketch, "E511", {"start": v(0.66, -1.28) * mm, "end": v(0.66, -1.28) * mm});
            skLineSegment(sketch, "E512", {"start": v(0.66, -1.28) * mm, "end": v(0.66, -1.29) * mm});
            skLineSegment(sketch, "E513", {"start": v(0.66, -1.29) * mm, "end": v(0.67, -1.3) * mm});
            skLineSegment(sketch, "E514", {"start": v(0.67, -1.3) * mm, "end": v(0.67, -1.3) * mm});
            skLineSegment(sketch, "E515", {"start": v(0.67, -1.3) * mm, "end": v(0.68, -1.3) * mm});
            skLineSegment(sketch, "E516", {"start": v(0.68, -1.3) * mm, "end": v(0.68, -1.31) * mm});
            skLineSegment(sketch, "E517", {"start": v(0.68, -1.31) * mm, "end": v(0.69, -1.32) * mm});
            skLineSegment(sketch, "E518", {"start": v(0.69, -1.32) * mm, "end": v(0.7, -1.32) * mm});
            skLineSegment(sketch, "E519", {"start": v(0.7, -1.32) * mm, "end": v(0.7, -1.33) * mm});
            skLineSegment(sketch, "E520", {"start": v(0.7, -1.33) * mm, "end": v(0.7, -1.33) * mm});
            skLineSegment(sketch, "E521", {"start": v(0.7, -1.33) * mm, "end": v(0.7, -1.34) * mm});
            skLineSegment(sketch, "E522", {"start": v(0.7, -1.34) * mm, "end": v(0.7, -1.35) * mm});
            skLineSegment(sketch, "E523", {"start": v(0.7, -1.35) * mm, "end": v(0.71, -1.35) * mm});
            skLineSegment(sketch, "E524", {"start": v(0.71, -1.35) * mm, "end": v(0.72, -1.36) * mm});
            skLineSegment(sketch, "E525", {"start": v(0.72, -1.36) * mm, "end": v(0.72, -1.37) * mm});
            skLineSegment(sketch, "E526", {"start": v(0.72, -1.37) * mm, "end": v(0.73, -1.37) * mm});
            skLineSegment(sketch, "E527", {"start": v(0.73, -1.37) * mm, "end": v(0.74, -1.38) * mm});
            skLineSegment(sketch, "E528", {"start": v(0.74, -1.38) * mm, "end": v(0.74, -1.39) * mm});
            skLineSegment(sketch, "E529", {"start": v(0.74, -1.39) * mm, "end": v(0.75, -1.4) * mm});
            skLineSegment(sketch, "E530", {"start": v(0.75, -1.4) * mm, "end": v(0.76, -1.4) * mm});
            skLineSegment(sketch, "E531", {"start": v(0.76, -1.4) * mm, "end": v(0.77, -1.4) * mm});
            skLineSegment(sketch, "E532", {"start": v(0.77, -1.4) * mm, "end": v(0.78, -1.41) * mm});
            skLineSegment(sketch, "E533", {"start": v(0.78, -1.41) * mm, "end": v(0.8, -1.42) * mm});
            skLineSegment(sketch, "E534", {"start": v(0.8, -1.42) * mm, "end": v(0.8, -1.42) * mm});
            skLineSegment(sketch, "E535", {"start": v(0.8, -1.42) * mm, "end": v(0.82, -1.43) * mm});
            skLineSegment(sketch, "E536", {"start": v(0.82, -1.43) * mm, "end": v(0.83, -1.44) * mm});
            skLineSegment(sketch, "E537", {"start": v(0.83, -1.44) * mm, "end": v(0.85, -1.45) * mm});
            skLineSegment(sketch, "E538", {"start": v(0.85, -1.45) * mm, "end": v(0.87, -1.46) * mm});
            skLineSegment(sketch, "E539", {"start": v(0.87, -1.46) * mm, "end": v(0.9, -1.47) * mm});
            skLineSegment(sketch, "E540", {"start": v(0.9, -1.47) * mm, "end": v(0.92, -1.48) * mm});
            skLineSegment(sketch, "E541", {"start": v(0.92, -1.48) * mm, "end": v(0.95, -1.5) * mm});
            skLineSegment(sketch, "E542", {"start": v(0.95, -1.5) * mm, "end": v(0.98, -1.5) * mm});
            skArc(sketch, "E543", {"start": v(0.98, -1.5) * mm, "mid": v(1.07, -1.44) * mm, "end": v(1.16, -1.38) * mm});
            skLineSegment(sketch, "E544", {"start": v(1.16, -1.38) * mm, "end": v(1.16, -1.34) * mm});
            skLineSegment(sketch, "E545", {"start": v(1.16, -1.34) * mm, "end": v(1.15, -1.3) * mm});
            skLineSegment(sketch, "E546", {"start": v(1.15, -1.3) * mm, "end": v(1.15, -1.28) * mm});
            skLineSegment(sketch, "E547", {"start": v(1.15, -1.28) * mm, "end": v(1.15, -1.25) * mm});
            skLineSegment(sketch, "E548", {"start": v(1.15, -1.25) * mm, "end": v(1.14, -1.23) * mm});
            skLineSegment(sketch, "E549", {"start": v(1.14, -1.23) * mm, "end": v(1.14, -1.21) * mm});
            skLineSegment(sketch, "E550", {"start": v(1.14, -1.21) * mm, "end": v(1.14, -1.2) * mm});
            skLineSegment(sketch, "E551", {"start": v(1.14, -1.2) * mm, "end": v(1.13, -1.18) * mm});
            skLineSegment(sketch, "E552", {"start": v(1.13, -1.18) * mm, "end": v(1.13, -1.17) * mm});
            skLineSegment(sketch, "E553", {"start": v(1.13, -1.17) * mm, "end": v(1.13, -1.15) * mm});
            skLineSegment(sketch, "E554", {"start": v(1.13, -1.15) * mm, "end": v(1.12, -1.14) * mm});
            skLineSegment(sketch, "E555", {"start": v(1.12, -1.14) * mm, "end": v(1.12, -1.13) * mm});
            skLineSegment(sketch, "E556", {"start": v(1.12, -1.13) * mm, "end": v(1.12, -1.12) * mm});
            skLineSegment(sketch, "E557", {"start": v(1.12, -1.12) * mm, "end": v(1.11, -1.11) * mm});
            skLineSegment(sketch, "E558", {"start": v(1.11, -1.11) * mm, "end": v(1.1, -1.1) * mm});
            skLineSegment(sketch, "E559", {"start": v(1.1, -1.1) * mm, "end": v(1.1, -1.1) * mm});
            skLineSegment(sketch, "E560", {"start": v(1.1, -1.1) * mm, "end": v(1.1, -1.09) * mm});
            skLineSegment(sketch, "E561", {"start": v(1.1, -1.09) * mm, "end": v(1.1, -1.08) * mm});
            skLineSegment(sketch, "E562", {"start": v(1.1, -1.08) * mm, "end": v(1.1, -1.07) * mm});
            skLineSegment(sketch, "E563", {"start": v(1.1, -1.07) * mm, "end": v(1.09, -1.07) * mm});
            skLineSegment(sketch, "E564", {"start": v(1.09, -1.07) * mm, "end": v(1.08, -1.06) * mm});
            skLineSegment(sketch, "E565", {"start": v(1.08, -1.06) * mm, "end": v(1.08, -1.05) * mm});
            skLineSegment(sketch, "E566", {"start": v(1.08, -1.05) * mm, "end": v(1.07, -1.05) * mm});
            skLineSegment(sketch, "E567", {"start": v(1.07, -1.05) * mm, "end": v(1.07, -1.04) * mm});
            skLineSegment(sketch, "E568", {"start": v(1.07, -1.04) * mm, "end": v(1.06, -1.04) * mm});
            skLineSegment(sketch, "E569", {"start": v(1.06, -1.04) * mm, "end": v(1.06, -1.03) * mm});
            skLineSegment(sketch, "E570", {"start": v(1.06, -1.03) * mm, "end": v(1.06, -1.03) * mm});
            skLineSegment(sketch, "E571", {"start": v(1.06, -1.03) * mm, "end": v(1.05, -1.02) * mm});
            skLineSegment(sketch, "E572", {"start": v(1.05, -1.02) * mm, "end": v(1.05, -1.02) * mm});
            skLineSegment(sketch, "E573", {"start": v(1.05, -1.02) * mm, "end": v(1.05, -1.01) * mm});
            skLineSegment(sketch, "E574", {"start": v(1.05, -1.01) * mm, "end": v(1.04, -1) * mm});
            skLineSegment(sketch, "E575", {"start": v(1.04, -1) * mm, "end": v(1.04, -1) * mm});
            skLineSegment(sketch, "E576", {"start": v(1.04, -1) * mm, "end": v(1.03, -1) * mm});
            skLineSegment(sketch, "E577", {"start": v(1.03, -1) * mm, "end": v(1.03, -1) * mm});
            skLineSegment(sketch, "E578", {"start": v(1.03, -1) * mm, "end": v(1.03, -0.99) * mm});
            skLineSegment(sketch, "E579", {"start": v(1.03, -0.99) * mm, "end": v(1.02, -0.98) * mm});
            skLineSegment(sketch, "E580", {"start": v(1.02, -0.98) * mm, "end": v(1.02, -0.98) * mm});
            skLineSegment(sketch, "E581", {"start": v(1.02, -0.98) * mm, "end": v(1.02, -0.97) * mm});
            skLineSegment(sketch, "E582", {"start": v(1.02, -0.97) * mm, "end": v(0.94, -0.87) * mm});
            skArc(sketch, "E583", {"start": v(0.94, -0.87) * mm, "mid": v(0.92, -0.8) * mm, "end": v(0.94, -0.75) * mm});
            skArc(sketch, "E584", {"start": v(0.94, -0.75) * mm, "mid": v(0.98, -0.7) * mm, "end": v(1.01, -0.64) * mm});
            skArc(sketch, "E585", {"start": v(1.01, -0.64) * mm, "mid": v(1.06, -0.6) * mm, "end": v(1.13, -0.6) * mm});
            skLineSegment(sketch, "E586", {"start": v(1.13, -0.6) * mm, "end": v(1.26, -0.64) * mm});
            skLineSegment(sketch, "E587", {"start": v(1.26, -0.64) * mm, "end": v(1.26, -0.64) * mm});
            skLineSegment(sketch, "E588", {"start": v(1.26, -0.64) * mm, "end": v(1.27, -0.64) * mm});
            skLineSegment(sketch, "E589", {"start": v(1.27, -0.64) * mm, "end": v(1.27, -0.64) * mm});
            skLineSegment(sketch, "E590", {"start": v(1.27, -0.64) * mm, "end": v(1.28, -0.65) * mm});
            skLineSegment(sketch, "E591", {"start": v(1.28, -0.65) * mm, "end": v(1.28, -0.65) * mm});
            skLineSegment(sketch, "E592", {"start": v(1.28, -0.65) * mm, "end": v(1.29, -0.65) * mm});
            skLineSegment(sketch, "E593", {"start": v(1.29, -0.65) * mm, "end": v(1.3, -0.65) * mm});
            skLineSegment(sketch, "E594", {"start": v(1.3, -0.65) * mm, "end": v(1.3, -0.65) * mm});
            skLineSegment(sketch, "E595", {"start": v(1.3, -0.65) * mm, "end": v(1.3, -0.66) * mm});
            skLineSegment(sketch, "E596", {"start": v(1.3, -0.66) * mm, "end": v(1.31, -0.66) * mm});
            skLineSegment(sketch, "E597", {"start": v(1.31, -0.66) * mm, "end": v(1.32, -0.66) * mm});
            skLineSegment(sketch, "E598", {"start": v(1.32, -0.66) * mm, "end": v(1.32, -0.66) * mm});
            skLineSegment(sketch, "E599", {"start": v(1.32, -0.66) * mm, "end": v(1.33, -0.66) * mm});
            skLineSegment(sketch, "E600", {"start": v(1.33, -0.66) * mm, "end": v(1.34, -0.66) * mm});
            skLineSegment(sketch, "E601", {"start": v(1.34, -0.66) * mm, "end": v(1.34, -0.67) * mm});
            skLineSegment(sketch, "E602", {"start": v(1.34, -0.67) * mm, "end": v(1.35, -0.67) * mm});
            skLineSegment(sketch, "E603", {"start": v(1.35, -0.67) * mm, "end": v(1.36, -0.67) * mm});
            skLineSegment(sketch, "E604", {"start": v(1.36, -0.67) * mm, "end": v(1.36, -0.67) * mm});
            skLineSegment(sketch, "E605", {"start": v(1.36, -0.67) * mm, "end": v(1.37, -0.68) * mm});
            skLineSegment(sketch, "E606", {"start": v(1.37, -0.68) * mm, "end": v(1.38, -0.68) * mm});
            skLineSegment(sketch, "E607", {"start": v(1.38, -0.68) * mm, "end": v(1.39, -0.68) * mm});
            skLineSegment(sketch, "E608", {"start": v(1.39, -0.68) * mm, "end": v(1.4, -0.68) * mm});
            skLineSegment(sketch, "E609", {"start": v(1.4, -0.68) * mm, "end": v(1.4, -0.68) * mm});
            skLineSegment(sketch, "E610", {"start": v(1.4, -0.68) * mm, "end": v(1.42, -0.68) * mm});
            skLineSegment(sketch, "E611", {"start": v(1.42, -0.68) * mm, "end": v(1.43, -0.68) * mm});
            skLineSegment(sketch, "E612", {"start": v(1.43, -0.68) * mm, "end": v(1.44, -0.68) * mm});
            skLineSegment(sketch, "E613", {"start": v(1.44, -0.68) * mm, "end": v(1.45, -0.68) * mm});
            skLineSegment(sketch, "E614", {"start": v(1.45, -0.68) * mm, "end": v(1.46, -0.68) * mm});
            skLineSegment(sketch, "E615", {"start": v(1.46, -0.68) * mm, "end": v(1.47, -0.68) * mm});
            skLineSegment(sketch, "E616", {"start": v(1.47, -0.68) * mm, "end": v(1.49, -0.68) * mm});
            skLineSegment(sketch, "E617", {"start": v(1.49, -0.68) * mm, "end": v(1.5, -0.68) * mm});
            skLineSegment(sketch, "E618", {"start": v(1.5, -0.68) * mm, "end": v(1.52, -0.68) * mm});
            skLineSegment(sketch, "E619", {"start": v(1.52, -0.68) * mm, "end": v(1.54, -0.67) * mm});
            skLineSegment(sketch, "E620", {"start": v(1.54, -0.67) * mm, "end": v(1.56, -0.67) * mm});
            skLineSegment(sketch, "E621", {"start": v(1.56, -0.67) * mm, "end": v(1.59, -0.67) * mm});
            skLineSegment(sketch, "E622", {"start": v(1.59, -0.67) * mm, "end": v(1.62, -0.66) * mm});
            skLineSegment(sketch, "E623", {"start": v(1.62, -0.66) * mm, "end": v(1.65, -0.65) * mm});
            skLineSegment(sketch, "E624", {"start": v(1.65, -0.65) * mm, "end": v(1.68, -0.64) * mm});
            skArc(sketch, "E625", {"start": v(1.68, -0.64) * mm, "mid": v(1.72, -0.54) * mm, "end": v(1.75, -0.43) * mm});
            skLineSegment(sketch, "E626", {"start": v(1.75, -0.43) * mm, "end": v(1.73, -0.4) * mm});
            skLineSegment(sketch, "E627", {"start": v(1.73, -0.4) * mm, "end": v(1.7, -0.38) * mm});
            skLineSegment(sketch, "E628", {"start": v(1.7, -0.38) * mm, "end": v(1.68, -0.36) * mm});
            skLineSegment(sketch, "E629", {"start": v(1.68, -0.36) * mm, "end": v(1.66, -0.34) * mm});
            skLineSegment(sketch, "E630", {"start": v(1.66, -0.34) * mm, "end": v(1.65, -0.32) * mm});
            skLineSegment(sketch, "E631", {"start": v(1.65, -0.32) * mm, "end": v(1.63, -0.3) * mm});
            skLineSegment(sketch, "E632", {"start": v(1.63, -0.3) * mm, "end": v(1.62, -0.3) * mm});
            skLineSegment(sketch, "E633", {"start": v(1.62, -0.3) * mm, "end": v(1.61, -0.29) * mm});
            skLineSegment(sketch, "E634", {"start": v(1.61, -0.29) * mm, "end": v(1.6, -0.28) * mm});
            skLineSegment(sketch, "E635", {"start": v(1.6, -0.28) * mm, "end": v(1.59, -0.27) * mm});
            skLineSegment(sketch, "E636", {"start": v(1.59, -0.27) * mm, "end": v(1.58, -0.26) * mm});
            skLineSegment(sketch, "E637", {"start": v(1.58, -0.26) * mm, "end": v(1.57, -0.26) * mm});
            skLineSegment(sketch, "E638", {"start": v(1.57, -0.26) * mm, "end": v(1.56, -0.25) * mm});
            skLineSegment(sketch, "E639", {"start": v(1.56, -0.25) * mm, "end": v(1.55, -0.25) * mm});
            skLineSegment(sketch, "E640", {"start": v(1.55, -0.25) * mm, "end": v(1.54, -0.24) * mm});
            skLineSegment(sketch, "E641", {"start": v(1.54, -0.24) * mm, "end": v(1.54, -0.24) * mm});
            skLineSegment(sketch, "E642", {"start": v(1.54, -0.24) * mm, "end": v(1.53, -0.23) * mm});
            skLineSegment(sketch, "E643", {"start": v(1.53, -0.23) * mm, "end": v(1.52, -0.23) * mm});
            skLineSegment(sketch, "E644", {"start": v(1.52, -0.23) * mm, "end": v(1.51, -0.23) * mm});
            skLineSegment(sketch, "E645", {"start": v(1.51, -0.23) * mm, "end": v(1.5, -0.22) * mm});
            skLineSegment(sketch, "E646", {"start": v(1.5, -0.22) * mm, "end": v(1.5, -0.22) * mm});
            skLineSegment(sketch, "E647", {"start": v(1.5, -0.22) * mm, "end": v(1.49, -0.22) * mm});
            skLineSegment(sketch, "E648", {"start": v(1.49, -0.22) * mm, "end": v(1.48, -0.22) * mm});
            skLineSegment(sketch, "E649", {"start": v(1.48, -0.22) * mm, "end": v(1.48, -0.22) * mm});
            skLineSegment(sketch, "E650", {"start": v(1.48, -0.22) * mm, "end": v(1.47, -0.21) * mm});
            skLineSegment(sketch, "E651", {"start": v(1.47, -0.21) * mm, "end": v(1.46, -0.21) * mm});
            skLineSegment(sketch, "E652", {"start": v(1.46, -0.21) * mm, "end": v(1.46, -0.2) * mm});
            skLineSegment(sketch, "E653", {"start": v(1.46, -0.2) * mm, "end": v(1.45, -0.2) * mm});
            skLineSegment(sketch, "E654", {"start": v(1.45, -0.2) * mm, "end": v(1.45, -0.2) * mm});
            skLineSegment(sketch, "E655", {"start": v(1.45, -0.2) * mm, "end": v(1.44, -0.2) * mm});
            skLineSegment(sketch, "E656", {"start": v(1.44, -0.2) * mm, "end": v(1.44, -0.2) * mm});
            skLineSegment(sketch, "E657", {"start": v(1.44, -0.2) * mm, "end": v(1.43, -0.2) * mm});
            skLineSegment(sketch, "E658", {"start": v(1.43, -0.2) * mm, "end": v(1.43, -0.2) * mm});
            skLineSegment(sketch, "E659", {"start": v(1.43, -0.2) * mm, "end": v(1.42, -0.2) * mm});
            skLineSegment(sketch, "E660", {"start": v(1.42, -0.2) * mm, "end": v(1.42, -0.2) * mm});
            skLineSegment(sketch, "E661", {"start": v(1.42, -0.2) * mm, "end": v(1.41, -0.2) * mm});
            skLineSegment(sketch, "E662", {"start": v(1.41, -0.2) * mm, "end": v(1.4, -0.2) * mm});
            skLineSegment(sketch, "E663", {"start": v(1.4, -0.2) * mm, "end": v(1.4, -0.2) * mm});
            skLineSegment(sketch, "E664", {"start": v(1.4, -0.2) * mm, "end": v(1.27, -0.15) * mm});
            skArc(sketch, "E665", {"start": v(1.27, -0.15) * mm, "mid": v(1.22, -0.11) * mm, "end": v(1.2, -0.05) * mm});
            skArc(sketch, "E666", {"start": v(1.2, -0.05) * mm, "mid": v(1.2, 0.01) * mm, "end": v(1.2, 0.08) * mm});
            skArc(sketch, "E667", {"start": v(1.2, 0.08) * mm, "mid": v(1.21, 0.14) * mm, "end": v(1.27, 0.18) * mm});
            skLineSegment(sketch, "E668", {"start": v(1.27, 0.18) * mm, "end": v(1.4, 0.22) * mm});
            skLineSegment(sketch, "E669", {"start": v(1.4, 0.22) * mm, "end": v(1.4, 0.22) * mm});
            skLineSegment(sketch, "E670", {"start": v(1.4, 0.22) * mm, "end": v(1.4, 0.23) * mm});
            skLineSegment(sketch, "E671", {"start": v(1.4, 0.23) * mm, "end": v(1.41, 0.23) * mm});
            skLineSegment(sketch, "E672", {"start": v(1.41, 0.23) * mm, "end": v(1.42, 0.23) * mm});
            skLineSegment(sketch, "E673", {"start": v(1.42, 0.23) * mm, "end": v(1.42, 0.23) * mm});
            skLineSegment(sketch, "E674", {"start": v(1.42, 0.23) * mm, "end": v(1.43, 0.23) * mm});
            skLineSegment(sketch, "E675", {"start": v(1.43, 0.23) * mm, "end": v(1.43, 0.23) * mm});
            skLineSegment(sketch, "E676", {"start": v(1.43, 0.23) * mm, "end": v(1.44, 0.24) * mm});
            skLineSegment(sketch, "E677", {"start": v(1.44, 0.24) * mm, "end": v(1.44, 0.24) * mm});
            skLineSegment(sketch, "E678", {"start": v(1.44, 0.24) * mm, "end": v(1.45, 0.24) * mm});
            skLineSegment(sketch, "E679", {"start": v(1.45, 0.24) * mm, "end": v(1.45, 0.24) * mm});
            skLineSegment(sketch, "E680", {"start": v(1.45, 0.24) * mm, "end": v(1.46, 0.24) * mm});
            skLineSegment(sketch, "E681", {"start": v(1.46, 0.24) * mm, "end": v(1.46, 0.25) * mm});
            skLineSegment(sketch, "E682", {"start": v(1.46, 0.25) * mm, "end": v(1.47, 0.25) * mm});
            skLineSegment(sketch, "E683", {"start": v(1.47, 0.25) * mm, "end": v(1.48, 0.25) * mm});
            skLineSegment(sketch, "E684", {"start": v(1.48, 0.25) * mm, "end": v(1.48, 0.25) * mm});
            skLineSegment(sketch, "E685", {"start": v(1.48, 0.25) * mm, "end": v(1.5, 0.25) * mm});
            skLineSegment(sketch, "E686", {"start": v(1.5, 0.25) * mm, "end": v(1.5, 0.26) * mm});
            skLineSegment(sketch, "E687", {"start": v(1.5, 0.26) * mm, "end": v(1.5, 0.26) * mm});
            skLineSegment(sketch, "E688", {"start": v(1.5, 0.26) * mm, "end": v(1.51, 0.26) * mm});
            skLineSegment(sketch, "E689", {"start": v(1.51, 0.26) * mm, "end": v(1.52, 0.27) * mm});
            skLineSegment(sketch, "E690", {"start": v(1.52, 0.27) * mm, "end": v(1.53, 0.27) * mm});
            skLineSegment(sketch, "E691", {"start": v(1.53, 0.27) * mm, "end": v(1.54, 0.27) * mm});
            skLineSegment(sketch, "E692", {"start": v(1.54, 0.27) * mm, "end": v(1.55, 0.28) * mm});
            skLineSegment(sketch, "E693", {"start": v(1.55, 0.28) * mm, "end": v(1.56, 0.28) * mm});
            skLineSegment(sketch, "E694", {"start": v(1.56, 0.28) * mm, "end": v(1.56, 0.3) * mm});
            skLineSegment(sketch, "E695", {"start": v(1.56, 0.3) * mm, "end": v(1.57, 0.3) * mm});
            skLineSegment(sketch, "E696", {"start": v(1.57, 0.3) * mm, "end": v(1.58, 0.3) * mm});
            skLineSegment(sketch, "E697", {"start": v(1.58, 0.3) * mm, "end": v(1.6, 0.31) * mm});
            skLineSegment(sketch, "E698", {"start": v(1.6, 0.31) * mm, "end": v(1.6, 0.32) * mm});
            skLineSegment(sketch, "E699", {"start": v(1.6, 0.32) * mm, "end": v(1.61, 0.33) * mm});
            skLineSegment(sketch, "E700", {"start": v(1.61, 0.33) * mm, "end": v(1.63, 0.35) * mm});
            skLineSegment(sketch, "E701", {"start": v(1.63, 0.35) * mm, "end": v(1.64, 0.36) * mm});
            skLineSegment(sketch, "E702", {"start": v(1.64, 0.36) * mm, "end": v(1.66, 0.37) * mm});
            skLineSegment(sketch, "E703", {"start": v(1.66, 0.37) * mm, "end": v(1.67, 0.4) * mm});
            skLineSegment(sketch, "E704", {"start": v(1.67, 0.4) * mm, "end": v(1.7, 0.42) * mm});
            skLineSegment(sketch, "E705", {"start": v(1.7, 0.42) * mm, "end": v(1.72, 0.44) * mm});
            skLineSegment(sketch, "E706", {"start": v(1.72, 0.44) * mm, "end": v(1.74, 0.47) * mm});
            skArc(sketch, "E707", {"start": v(1.74, 0.47) * mm, "mid": v(1.7, 0.57) * mm, "end": v(1.67, 0.68) * mm});
            skLineSegment(sketch, "E708", {"start": v(1.67, 0.68) * mm, "end": v(1.63, 0.69) * mm});
            skLineSegment(sketch, "E709", {"start": v(1.63, 0.69) * mm, "end": v(1.6, 0.7) * mm});
            skLineSegment(sketch, "E710", {"start": v(1.6, 0.7) * mm, "end": v(1.57, 0.7) * mm});
            skLineSegment(sketch, "E711", {"start": v(1.57, 0.7) * mm, "end": v(1.54, 0.7) * mm});
            skLineSegment(sketch, "E712", {"start": v(1.54, 0.7) * mm, "end": v(1.52, 0.7) * mm});
            skLineSegment(sketch, "E713", {"start": v(1.52, 0.7) * mm, "end": v(1.5, 0.71) * mm});
            skLineSegment(sketch, "E714", {"start": v(1.5, 0.71) * mm, "end": v(1.49, 0.71) * mm});
            skLineSegment(sketch, "E715", {"start": v(1.49, 0.71) * mm, "end": v(1.47, 0.71) * mm});
            skLineSegment(sketch, "E716", {"start": v(1.47, 0.71) * mm, "end": v(1.46, 0.71) * mm});
            skLineSegment(sketch, "E717", {"start": v(1.46, 0.71) * mm, "end": v(1.44, 0.71) * mm});
            skLineSegment(sketch, "E718", {"start": v(1.44, 0.71) * mm, "end": v(1.43, 0.72) * mm});
            skLineSegment(sketch, "E719", {"start": v(1.43, 0.72) * mm, "end": v(1.42, 0.72) * mm});
            skLineSegment(sketch, "E720", {"start": v(1.42, 0.72) * mm, "end": v(1.41, 0.72) * mm});
            skLineSegment(sketch, "E721", {"start": v(1.41, 0.72) * mm, "end": v(1.4, 0.71) * mm});
            skLineSegment(sketch, "E722", {"start": v(1.4, 0.71) * mm, "end": v(1.4, 0.71) * mm});
            skLineSegment(sketch, "E723", {"start": v(1.4, 0.71) * mm, "end": v(1.38, 0.71) * mm});
            skLineSegment(sketch, "E724", {"start": v(1.38, 0.71) * mm, "end": v(1.37, 0.71) * mm});
            skLineSegment(sketch, "E725", {"start": v(1.37, 0.71) * mm, "end": v(1.36, 0.7) * mm});
            skLineSegment(sketch, "E726", {"start": v(1.36, 0.7) * mm, "end": v(1.36, 0.7) * mm});
            skLineSegment(sketch, "E727", {"start": v(1.36, 0.7) * mm, "end": v(1.35, 0.7) * mm});
            skLineSegment(sketch, "E728", {"start": v(1.35, 0.7) * mm, "end": v(1.34, 0.7) * mm});
            skLineSegment(sketch, "E729", {"start": v(1.34, 0.7) * mm, "end": v(1.33, 0.7) * mm});
            skLineSegment(sketch, "E730", {"start": v(1.33, 0.7) * mm, "end": v(1.33, 0.7) * mm});
            skLineSegment(sketch, "E731", {"start": v(1.33, 0.7) * mm, "end": v(1.32, 0.7) * mm});
            skLineSegment(sketch, "E732", {"start": v(1.32, 0.7) * mm, "end": v(1.31, 0.7) * mm});
            skLineSegment(sketch, "E733", {"start": v(1.31, 0.7) * mm, "end": v(1.3, 0.69) * mm});
            skLineSegment(sketch, "E734", {"start": v(1.3, 0.69) * mm, "end": v(1.3, 0.69) * mm});
            skLineSegment(sketch, "E735", {"start": v(1.3, 0.69) * mm, "end": v(1.3, 0.68) * mm});
            skLineSegment(sketch, "E736", {"start": v(1.3, 0.68) * mm, "end": v(1.29, 0.68) * mm});
            skLineSegment(sketch, "E737", {"start": v(1.29, 0.68) * mm, "end": v(1.28, 0.68) * mm});
            skLineSegment(sketch, "E738", {"start": v(1.28, 0.68) * mm, "end": v(1.28, 0.68) * mm});
            skLineSegment(sketch, "E739", {"start": v(1.28, 0.68) * mm, "end": v(1.27, 0.68) * mm});
            skLineSegment(sketch, "E740", {"start": v(1.27, 0.68) * mm, "end": v(1.27, 0.68) * mm});
            skLineSegment(sketch, "E741", {"start": v(1.27, 0.68) * mm, "end": v(1.26, 0.67) * mm});
            skLineSegment(sketch, "E742", {"start": v(1.26, 0.67) * mm, "end": v(1.26, 0.67) * mm});
            skLineSegment(sketch, "E743", {"start": v(1.26, 0.67) * mm, "end": v(1.25, 0.67) * mm});
            skLineSegment(sketch, "E744", {"start": v(1.25, 0.67) * mm, "end": v(1.25, 0.67) * mm});
            skLineSegment(sketch, "E745", {"start": v(1.25, 0.67) * mm, "end": v(1.24, 0.67) * mm});
            skLineSegment(sketch, "E746", {"start": v(1.24, 0.67) * mm, "end": v(1.24, 0.67) * mm});
            skLineSegment(sketch, "E747", {"start": v(1.24, 0.67) * mm, "end": v(1.12, 0.62) * mm});
            skArc(sketch, "E748", {"start": v(1.12, 0.62) * mm, "mid": v(1.05, 0.62) * mm, "end": v(1, 0.66) * mm});
            skArc(sketch, "E749", {"start": v(1, 0.66) * mm, "mid": v(0.96, 0.72) * mm, "end": v(0.92, 0.77) * mm});
            skArc(sketch, "E750", {"start": v(0.92, 0.77) * mm, "mid": v(0.9, 0.83) * mm, "end": v(0.92, 0.89) * mm});
            skLineSegment(sketch, "E751", {"start": v(0.92, 0.89) * mm, "end": v(1, 1) * mm});
            skLineSegment(sketch, "E752", {"start": v(1, 1) * mm, "end": v(1, 1) * mm});
            skLineSegment(sketch, "E753", {"start": v(1, 1) * mm, "end": v(1, 1.01) * mm});
            skLineSegment(sketch, "E754", {"start": v(1, 1.01) * mm, "end": v(1.01, 1.02) * mm});
            skLineSegment(sketch, "E755", {"start": v(1.01, 1.02) * mm, "end": v(1.01, 1.02) * mm});
            skLineSegment(sketch, "E756", {"start": v(1.01, 1.02) * mm, "end": v(1.02, 1.03) * mm});
            skLineSegment(sketch, "E757", {"start": v(1.02, 1.03) * mm, "end": v(1.02, 1.03) * mm});
            skLineSegment(sketch, "E758", {"start": v(1.02, 1.03) * mm, "end": v(1.03, 1.04) * mm});
            skLineSegment(sketch, "E759", {"start": v(1.03, 1.04) * mm, "end": v(1.03, 1.04) * mm});
            skLineSegment(sketch, "E760", {"start": v(1.03, 1.04) * mm, "end": v(1.03, 1.05) * mm});
            skLineSegment(sketch, "E761", {"start": v(1.03, 1.05) * mm, "end": v(1.04, 1.05) * mm});
            skLineSegment(sketch, "E762", {"start": v(1.04, 1.05) * mm, "end": v(1.04, 1.06) * mm});
            skLineSegment(sketch, "E763", {"start": v(1.04, 1.06) * mm, "end": v(1.04, 1.06) * mm});
            skLineSegment(sketch, "E764", {"start": v(1.04, 1.06) * mm, "end": v(1.05, 1.07) * mm});
            skLineSegment(sketch, "E765", {"start": v(1.05, 1.07) * mm, "end": v(1.05, 1.08) * mm});
            skLineSegment(sketch, "E766", {"start": v(1.05, 1.08) * mm, "end": v(1.06, 1.08) * mm});
            skLineSegment(sketch, "E767", {"start": v(1.06, 1.08) * mm, "end": v(1.06, 1.09) * mm});
            skLineSegment(sketch, "E768", {"start": v(1.06, 1.09) * mm, "end": v(1.07, 1.1) * mm});
            skLineSegment(sketch, "E769", {"start": v(1.07, 1.1) * mm, "end": v(1.07, 1.1) * mm});
            skLineSegment(sketch, "E770", {"start": v(1.07, 1.1) * mm, "end": v(1.08, 1.11) * mm});
            skLineSegment(sketch, "E771", {"start": v(1.08, 1.11) * mm, "end": v(1.08, 1.12) * mm});
            skLineSegment(sketch, "E772", {"start": v(1.08, 1.12) * mm, "end": v(1.08, 1.13) * mm});
            skLineSegment(sketch, "E773", {"start": v(1.08, 1.13) * mm, "end": v(1.09, 1.14) * mm});
            skLineSegment(sketch, "E774", {"start": v(1.09, 1.14) * mm, "end": v(1.1, 1.14) * mm});
            skLineSegment(sketch, "E775", {"start": v(1.1, 1.14) * mm, "end": v(1.1, 1.16) * mm});
            skLineSegment(sketch, "E776", {"start": v(1.1, 1.16) * mm, "end": v(1.1, 1.17) * mm});
            skLineSegment(sketch, "E777", {"start": v(1.1, 1.17) * mm, "end": v(1.1, 1.18) * mm});
            skLineSegment(sketch, "E778", {"start": v(1.1, 1.18) * mm, "end": v(1.1, 1.2) * mm});
            skLineSegment(sketch, "E779", {"start": v(1.1, 1.2) * mm, "end": v(1.1, 1.2) * mm});
            skLineSegment(sketch, "E780", {"start": v(1.1, 1.2) * mm, "end": v(1.11, 1.22) * mm});
            skLineSegment(sketch, "E781", {"start": v(1.11, 1.22) * mm, "end": v(1.11, 1.24) * mm});
            skLineSegment(sketch, "E782", {"start": v(1.11, 1.24) * mm, "end": v(1.12, 1.25) * mm});
            skLineSegment(sketch, "E783", {"start": v(1.12, 1.25) * mm, "end": v(1.12, 1.28) * mm});
            skLineSegment(sketch, "E784", {"start": v(1.12, 1.28) * mm, "end": v(1.12, 1.3) * mm});
            skLineSegment(sketch, "E785", {"start": v(1.12, 1.3) * mm, "end": v(1.13, 1.33) * mm});
            skLineSegment(sketch, "E786", {"start": v(1.13, 1.33) * mm, "end": v(1.13, 1.37) * mm});
            skLineSegment(sketch, "E787", {"start": v(1.13, 1.37) * mm, "end": v(1.13, 1.4) * mm});
            skArc(sketch, "E788", {"start": v(1.13, 1.4) * mm, "mid": v(1.04, 1.47) * mm, "end": v(0.95, 1.53) * mm});
            skLineSegment(sketch, "E789", {"start": v(0.95, 1.53) * mm, "end": v(0.92, 1.52) * mm});
            skLineSegment(sketch, "E790", {"start": v(0.92, 1.52) * mm, "end": v(0.89, 1.5) * mm});
            skLineSegment(sketch, "E791", {"start": v(0.89, 1.5) * mm, "end": v(0.86, 1.49) * mm});
            skLineSegment(sketch, "E792", {"start": v(0.86, 1.49) * mm, "end": v(0.84, 1.48) * mm});
            skLineSegment(sketch, "E793", {"start": v(0.84, 1.48) * mm, "end": v(0.82, 1.47) * mm});
            skLineSegment(sketch, "E794", {"start": v(0.82, 1.47) * mm, "end": v(0.8, 1.46) * mm});
            skLineSegment(sketch, "E795", {"start": v(0.8, 1.46) * mm, "end": v(0.78, 1.45) * mm});
            skLineSegment(sketch, "E796", {"start": v(0.78, 1.45) * mm, "end": v(0.77, 1.44) * mm});
            skLineSegment(sketch, "E797", {"start": v(0.77, 1.44) * mm, "end": v(0.76, 1.43) * mm});
            skLineSegment(sketch, "E798", {"start": v(0.76, 1.43) * mm, "end": v(0.75, 1.43) * mm});
            skLineSegment(sketch, "E799", {"start": v(0.75, 1.43) * mm, "end": v(0.74, 1.42) * mm});
            skLineSegment(sketch, "E800", {"start": v(0.74, 1.42) * mm, "end": v(0.73, 1.41) * mm});
            skLineSegment(sketch, "E801", {"start": v(0.73, 1.41) * mm, "end": v(0.72, 1.4) * mm});
            skLineSegment(sketch, "E802", {"start": v(0.72, 1.4) * mm, "end": v(0.71, 1.4) * mm});
            skLineSegment(sketch, "E803", {"start": v(0.71, 1.4) * mm, "end": v(0.7, 1.4) * mm});
            skLineSegment(sketch, "E804", {"start": v(0.7, 1.4) * mm, "end": v(0.7, 1.39) * mm});
            skLineSegment(sketch, "E805", {"start": v(0.7, 1.39) * mm, "end": v(0.7, 1.38) * mm});
            skLineSegment(sketch, "E806", {"start": v(0.7, 1.38) * mm, "end": v(0.69, 1.37) * mm});
            skLineSegment(sketch, "E807", {"start": v(0.69, 1.37) * mm, "end": v(0.68, 1.37) * mm});
            skLineSegment(sketch, "E808", {"start": v(0.68, 1.37) * mm, "end": v(0.68, 1.36) * mm});
            skLineSegment(sketch, "E809", {"start": v(0.68, 1.36) * mm, "end": v(0.67, 1.35) * mm});
            skLineSegment(sketch, "E810", {"start": v(0.67, 1.35) * mm, "end": v(0.67, 1.35) * mm});
            skLineSegment(sketch, "E811", {"start": v(0.67, 1.35) * mm, "end": v(0.67, 1.34) * mm});
            skLineSegment(sketch, "E812", {"start": v(0.67, 1.34) * mm, "end": v(0.66, 1.34) * mm});
            skLineSegment(sketch, "E813", {"start": v(0.66, 1.34) * mm, "end": v(0.66, 1.33) * mm});
            skLineSegment(sketch, "E814", {"start": v(0.66, 1.33) * mm, "end": v(0.65, 1.33) * mm});
            skLineSegment(sketch, "E815", {"start": v(0.65, 1.33) * mm, "end": v(0.65, 1.32) * mm});
            skLineSegment(sketch, "E816", {"start": v(0.65, 1.32) * mm, "end": v(0.65, 1.32) * mm});
            skLineSegment(sketch, "E817", {"start": v(0.65, 1.32) * mm, "end": v(0.64, 1.31) * mm});
            skSolve(sketch);
        }
        {
            var Q0;
            Q0 = qSketchRegion(id + "F0", true);
            extrude(context, id + "F1", {"entities" : qUnion([Q0]), "depth" : 0.13 * mm});
        }
    });
